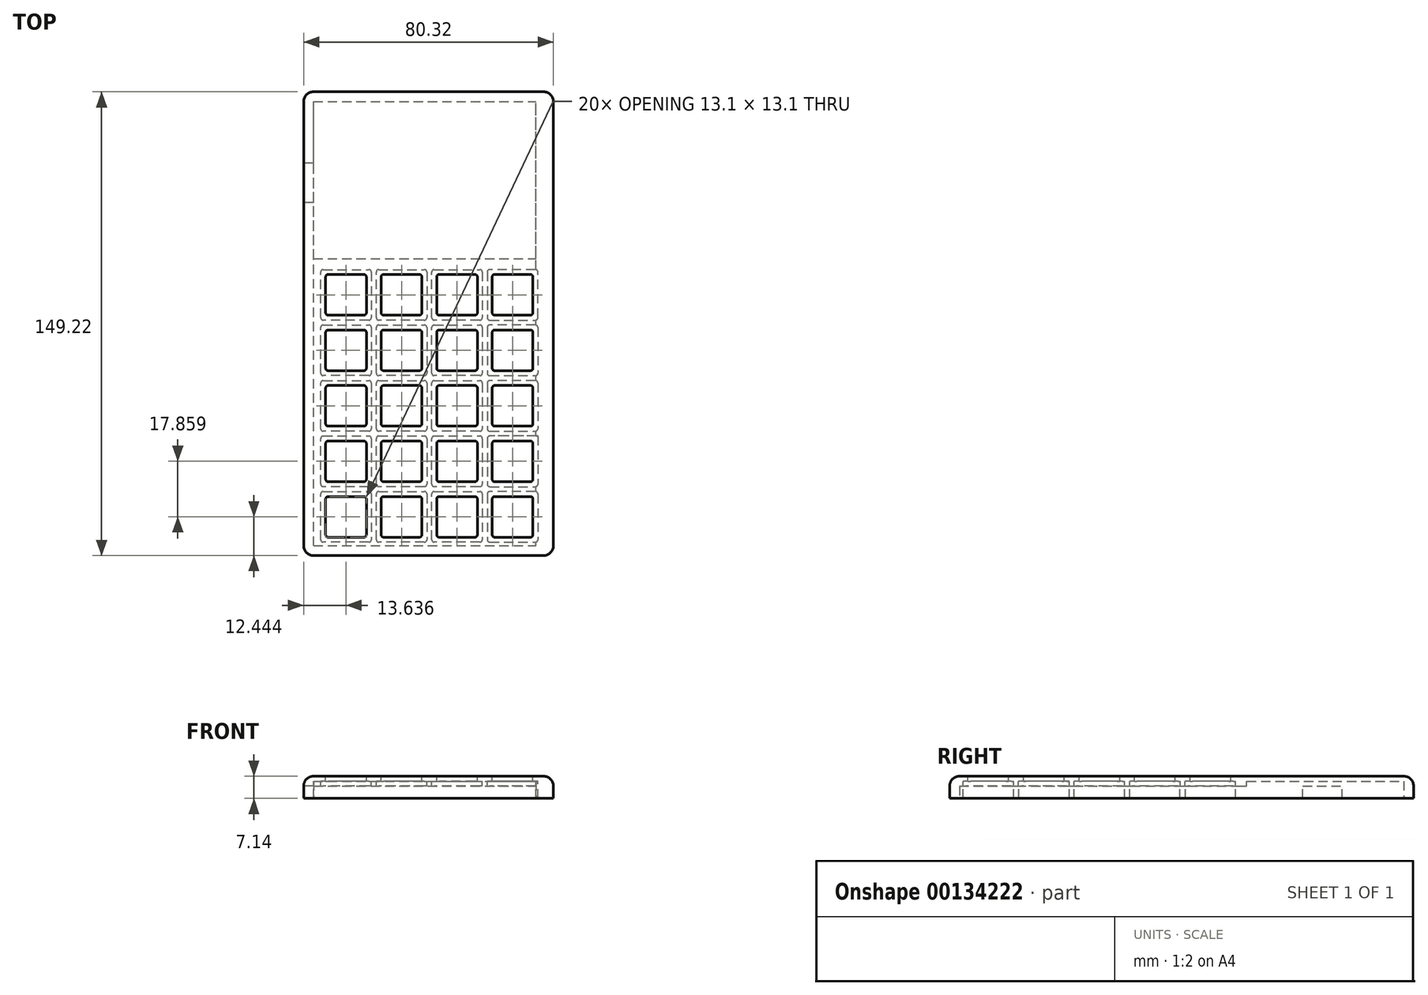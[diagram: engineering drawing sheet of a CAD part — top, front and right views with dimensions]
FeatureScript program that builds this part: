
annotation { "Feature Type Name" : "Feature", "Feature Type Description" : "" }
export const myFeature = defineFeature(function(context is Context, id is Id, definition is map)
    precondition{}
    {
        {
            var Q0;
            Q0=qCreatedBy(makeId("Top.planeOp"),FACE);
            var sketch = newSketch(context, id + "F0", { "sketchPlane" : qUnion([Q0])});
            skLineSegment(sketch, "E0.bottom", {"start": v(40.16, 74.61) * mm, "end": v(-40.16, 74.61) * mm});
            skLineSegment(sketch, "E0.top", {"start": v(40.16, -74.61) * mm, "end": v(-40.16, -74.61) * mm});
            skLineSegment(sketch, "E0.left", {"start": v(40.16, 74.61) * mm, "end": v(40.16, -74.61) * mm});
            skLineSegment(sketch, "E0.right", {"start": v(-40.16, 74.61) * mm, "end": v(-40.16, -74.61) * mm});
            skPoint(sketch, "E0.middle", {"position": v(0, 0) * mm});
            skSolve(sketch);
        }
        {
            var Q0;
            Q0 = qSketchRegion(id + "F0", true);
            extrude(context, id + "F1", {"entities" : qUnion([Q0]), "depth" : 7.14 * mm});
        }
        {
            var Q0;
            Q0=makeQuery(id+"F1.opExtrude","CAP_EDGE",EDGE,{"disambiguationData":[OSD([sQuery(id+"F0.wireOp",EDGE,"E0.right")])],"isStart":false});
            var Q1;
            Q1=makeQuery(id+"F1.opExtrude","CAP_EDGE",EDGE,{"disambiguationData":[OSD([sQuery(id+"F0.wireOp",EDGE,"E0.bottom")])],"isStart":false});
            var Q2;
            Q2=makeQuery(id+"F1.opExtrude","CAP_EDGE",EDGE,{"disambiguationData":[OSD([sQuery(id+"F0.wireOp",EDGE,"E0.left")])],"isStart":false});
            var Q3;
            Q3=makeQuery(id+"F1.opExtrude","CAP_EDGE",EDGE,{"disambiguationData":[OSD([sQuery(id+"F0.wireOp",EDGE,"E0.top")])],"isStart":false});
            fillet(context, id + "F2", {"entities" : qUnion([Q0, Q1, Q2, Q3]), "radius" : 3.17 * mm, "tangentPropagation" : true, "allowEdgeOverflow" : false});
        }
        {
            var Q0;
            Q0=makeQuery(id+"F1.opExtrude","SWEPT_EDGE",EDGE,{"disambiguationData":[OSD([sQuery(id+"F0.wireOp",EDGE,"E0.bottom"),sQuery(id+"F0.wireOp",EDGE,"E0.left")])]});
            var Q1;
            Q1=makeQuery(id+"F1.opExtrude","SWEPT_EDGE",EDGE,{"disambiguationData":[OSD([sQuery(id+"F0.wireOp",EDGE,"E0.top"),sQuery(id+"F0.wireOp",EDGE,"E0.left")])]});
            var Q2;
            Q2=makeQuery(id+"F1.opExtrude","SWEPT_EDGE",EDGE,{"disambiguationData":[OSD([sQuery(id+"F0.wireOp",EDGE,"E0.top"),sQuery(id+"F0.wireOp",EDGE,"E0.right")])]});
            var Q3;
            Q3=makeQuery(id+"F1.opExtrude","SWEPT_EDGE",EDGE,{"disambiguationData":[OSD([sQuery(id+"F0.wireOp",EDGE,"E0.bottom"),sQuery(id+"F0.wireOp",EDGE,"E0.right")])]});
            fillet(context, id + "F3", {"entities" : qUnion([Q0, Q1, Q2, Q3]), "radius" : 3.17 * mm, "tangentPropagation" : true, "allowEdgeOverflow" : false});
        }
        {
            var Q0;
            Q0=makeQuery(id+"F1.opExtrude","CAP_FACE",FACE,{"disambiguationData":[OSD([sQuery(id+"F0.wireOp",EDGE,"E0.bottom"),sQuery(id+"F0.wireOp",EDGE,"E0.top"),sQuery(id+"F0.wireOp",EDGE,"E0.left"),sQuery(id+"F0.wireOp",EDGE,"E0.right")])],"isStart":true});
            var sketch = newSketch(context, id + "F4", { "sketchPlane" : qUnion([Q0])});
            skLineSegment(sketch, "E1.0.0", {"start": v(40.16, -71.44) * mm, "end": v(40.16, 71.44) * mm});
            skArc(sketch, "E1.0.1", {"start": v(40.16, 71.44) * mm, "mid": v(39.23, 73.68) * mm, "end": v(36.99, 74.61) * mm});
            skLineSegment(sketch, "E1.0.2", {"start": v(36.99, 74.61) * mm, "end": v(-36.99, 74.61) * mm});
            skArc(sketch, "E1.0.3", {"start": v(-36.99, 74.61) * mm, "mid": v(-39.23, 73.68) * mm, "end": v(-40.16, 71.44) * mm});
            skLineSegment(sketch, "E1.0.4", {"start": v(-40.16, 71.44) * mm, "end": v(-40.16, -71.44) * mm});
            skArc(sketch, "E1.0.5", {"start": v(-40.16, -71.44) * mm, "mid": v(-39.23, -73.68) * mm, "end": v(-36.99, -74.61) * mm});
            skLineSegment(sketch, "E1.0.6", {"start": v(-36.99, -74.61) * mm, "end": v(36.99, -74.61) * mm});
            skArc(sketch, "E1.0.7", {"start": v(36.99, -74.61) * mm, "mid": v(39.23, -73.68) * mm, "end": v(40.16, -71.44) * mm});
            skLineSegment(sketch, "E2.bottom", {"start": v(-36.99, 71.44) * mm, "end": v(34.6, 71.44) * mm});
            skLineSegment(sketch, "E2.top", {"start": v(-36.99, -71.44) * mm, "end": v(34.6, -71.44) * mm});
            skLineSegment(sketch, "E2.left", {"start": v(-36.99, 71.44) * mm, "end": v(-36.99, -71.44) * mm});
            skLineSegment(sketch, "E2.right", {"start": v(34.6, 71.44) * mm, "end": v(34.6, -71.44) * mm});
            skSolve(sketch);
        }
        {
            var Q0;
            Q0=makeQuery(id+"F4.imprint","IMPRINT",FACE,{"disambiguationData":[TD([[makeQuery(id+"F4.imprint","IMPRINT",EDGE,{"derivedFrom":sQuery(id+"F4.wireOp",EDGE,"E2.bottom")}),-1.0]])]});
            extrude(context, id + "F5", {"entities" : qUnion([Q0]), "operationType" : NewBodyOperationType.REMOVE, "oppositeDirection" : true, "depth" : 5.56 * mm});
        }
        {
            var Q0;
            Q0=makeQuery(id+"F1.opExtrude","CAP_FACE",FACE,{"disambiguationData":[OSD([sQuery(id+"F0.wireOp",EDGE,"E0.bottom"),sQuery(id+"F0.wireOp",EDGE,"E0.top"),sQuery(id+"F0.wireOp",EDGE,"E0.left"),sQuery(id+"F0.wireOp",EDGE,"E0.right")])],"isStart":false});
            var sketch = newSketch(context, id + "F6", { "sketchPlane" : qUnion([Q0])});
            skLineSegment(sketch, "E3.0.0", {"start": v(-36.99, -71.44) * mm, "end": v(-36.99, -71.44) * mm});
            skLineSegment(sketch, "E3.0.1", {"start": v(-36.99, -71.44) * mm, "end": v(36.99, -71.44) * mm});
            skLineSegment(sketch, "E3.0.2", {"start": v(36.99, -71.44) * mm, "end": v(36.99, -71.44) * mm});
            skLineSegment(sketch, "E3.0.3", {"start": v(36.99, -71.44) * mm, "end": v(36.99, 71.44) * mm});
            skArc(sketch, "E3.0.4", {"start": v(35.08, 71.44) * mm, "mid": v(36.04, 71.7) * mm, "end": v(36.99, 71.44) * mm});
            skLineSegment(sketch, "E3.0.5", {"start": v(35.08, 71.44) * mm, "end": v(-35.08, 71.44) * mm});
            skArc(sketch, "E3.0.6", {"start": v(-36.99, 71.44) * mm, "mid": v(-36.04, 71.7) * mm, "end": v(-35.08, 71.44) * mm});
            skLineSegment(sketch, "E3.0.7", {"start": v(-36.99, 71.44) * mm, "end": v(-36.99, -71.44) * mm});
            skLineSegment(sketch, "E4.0.0", {"start": v(40.16, -71.44) * mm, "end": v(40.16, 71.44) * mm});
            skLineSegment(sketch, "E4.0.1", {"start": v(40.16, 71.44) * mm, "end": v(36.99, 71.44) * mm});
            skLineSegment(sketch, "E4.0.3", {"start": v(36.99, -71.44) * mm, "end": v(40.16, -71.44) * mm});
            skLineSegment(sketch, "E5.0.2", {"start": v(36.99, -71.44) * mm, "end": v(36.99, -74.61) * mm});
            skArc(sketch, "E5.0.3", {"start": v(36.99, -74.61) * mm, "mid": v(39.23, -73.68) * mm, "end": v(40.16, -71.44) * mm});
            skLineSegment(sketch, "E6.0.0", {"start": v(-36.99, -74.61) * mm, "end": v(36.99, -74.61) * mm});
            skLineSegment(sketch, "E6.0.1", {"start": v(36.99, -74.61) * mm, "end": v(36.99, -71.44) * mm});
            skLineSegment(sketch, "E6.0.3", {"start": v(-36.99, -71.44) * mm, "end": v(-36.99, -74.61) * mm});
            skLineSegment(sketch, "E7.0.2", {"start": v(-36.99, -71.44) * mm, "end": v(-40.16, -71.44) * mm});
            skArc(sketch, "E7.0.3", {"start": v(-40.16, -71.44) * mm, "mid": v(-39.23, -73.68) * mm, "end": v(-36.99, -74.61) * mm});
            skLineSegment(sketch, "E8.0.0", {"start": v(-40.16, -71.44) * mm, "end": v(-40.16, 71.44) * mm});
            skLineSegment(sketch, "E8.0.1", {"start": v(-40.16, -71.44) * mm, "end": v(-36.99, -71.44) * mm});
            skLineSegment(sketch, "E8.0.2", {"start": v(-36.99, -71.44) * mm, "end": v(-36.99, 71.44) * mm});
            skLineSegment(sketch, "E8.0.3", {"start": v(-36.99, 71.44) * mm, "end": v(-40.16, 71.44) * mm});
            skLineSegment(sketch, "E9.bottom", {"start": v(27.04, -74.61) * mm, "end": v(40.16, -74.61) * mm});
            skLineSegment(sketch, "E9.top", {"start": v(27.04, -62.17) * mm, "end": v(40.16, -62.17) * mm});
            skLineSegment(sketch, "E9.left", {"start": v(27.04, -74.61) * mm, "end": v(27.04, -62.17) * mm});
            skLineSegment(sketch, "E9.right", {"start": v(40.16, -74.61) * mm, "end": v(40.16, -62.17) * mm});
            skLineSegment(sketch, "E10.bottom", {"start": v(21.29, -68.71) * mm, "end": v(32.8, -68.71) * mm});
            skLineSegment(sketch, "E10.top", {"start": v(21.29, -55.62) * mm, "end": v(32.8, -55.62) * mm});
            skLineSegment(sketch, "E10.left", {"start": v(20.5, -67.92) * mm, "end": v(20.5, -56.41) * mm});
            skLineSegment(sketch, "E10.right", {"start": v(33.6, -67.92) * mm, "end": v(33.6, -56.41) * mm});
            skPoint(sketch, "E10.middle", {"position": v(27.04, -62.17) * mm});
            skPoint(sketch, "E11.visualSharp", {"position": v(20.5, -55.62) * mm});
            skArc(sketch, "E11.filletArc", {"start": v(21.29, -55.62) * mm, "mid": v(20.73, -55.85) * mm, "end": v(20.5, -56.41) * mm});
            skPoint(sketch, "E12.visualSharp", {"position": v(33.6, -55.62) * mm});
            skArc(sketch, "E12.filletArc", {"start": v(33.6, -56.41) * mm, "mid": v(33.36, -55.85) * mm, "end": v(32.8, -55.62) * mm});
            skPoint(sketch, "E13.visualSharp", {"position": v(33.6, -68.71) * mm});
            skArc(sketch, "E13.filletArc", {"start": v(32.8, -68.71) * mm, "mid": v(33.36, -68.48) * mm, "end": v(33.6, -67.92) * mm});
            skPoint(sketch, "E14.visualSharp", {"position": v(20.5, -68.71) * mm});
            skArc(sketch, "E14.filletArc", {"start": v(20.5, -67.92) * mm, "mid": v(20.73, -68.48) * mm, "end": v(21.29, -68.71) * mm});
            skLineSegment(sketch, "E15", {"start": v(27.04, -62.17) * mm, "end": v(18.31, -62.17) * mm});
            skLineSegment(sketch, "E16", {"start": v(18.31, -55.46) * mm, "end": v(18.31, -68.4) * mm, "construction": true});
            skLineSegment(sketch, "E17.1.0.0", {"start": v(2.64, -67.92) * mm, "end": v(2.64, -56.41) * mm});
            skArc(sketch, "E17.1.0.1", {"start": v(3.43, -55.62) * mm, "mid": v(2.87, -55.85) * mm, "end": v(2.64, -56.41) * mm});
            skLineSegment(sketch, "E17.1.0.2", {"start": v(3.43, -55.62) * mm, "end": v(14.94, -55.62) * mm});
            skArc(sketch, "E17.1.0.3", {"start": v(15.74, -56.41) * mm, "mid": v(15.5, -55.85) * mm, "end": v(14.94, -55.62) * mm});
            skLineSegment(sketch, "E17.1.0.4", {"start": v(15.74, -67.92) * mm, "end": v(15.74, -56.41) * mm});
            skArc(sketch, "E17.1.0.5", {"start": v(14.94, -68.71) * mm, "mid": v(15.5, -68.48) * mm, "end": v(15.74, -67.92) * mm});
            skLineSegment(sketch, "E17.1.0.6", {"start": v(3.43, -68.71) * mm, "end": v(14.94, -68.71) * mm});
            skArc(sketch, "E17.1.0.7", {"start": v(2.64, -67.92) * mm, "mid": v(2.87, -68.48) * mm, "end": v(3.43, -68.71) * mm});
            skLineSegment(sketch, "E17.2.0.0", {"start": v(-15.22, -67.92) * mm, "end": v(-15.22, -56.41) * mm});
            skArc(sketch, "E17.2.0.1", {"start": v(-14.42, -55.62) * mm, "mid": v(-14.98, -55.85) * mm, "end": v(-15.22, -56.41) * mm});
            skLineSegment(sketch, "E17.2.0.2", {"start": v(-14.42, -55.62) * mm, "end": v(-2.91, -55.62) * mm});
            skArc(sketch, "E17.2.0.3", {"start": v(-2.12, -56.41) * mm, "mid": v(-2.35, -55.85) * mm, "end": v(-2.91, -55.62) * mm});
            skLineSegment(sketch, "E17.2.0.4", {"start": v(-2.12, -67.92) * mm, "end": v(-2.12, -56.41) * mm});
            skArc(sketch, "E17.2.0.5", {"start": v(-2.91, -68.71) * mm, "mid": v(-2.35, -68.48) * mm, "end": v(-2.12, -67.92) * mm});
            skLineSegment(sketch, "E17.2.0.6", {"start": v(-14.42, -68.71) * mm, "end": v(-2.91, -68.71) * mm});
            skArc(sketch, "E17.2.0.7", {"start": v(-15.22, -67.92) * mm, "mid": v(-14.98, -68.48) * mm, "end": v(-14.42, -68.71) * mm});
            skLineSegment(sketch, "E17.3.0.0", {"start": v(-33.07, -67.92) * mm, "end": v(-33.07, -56.41) * mm});
            skArc(sketch, "E17.3.0.1", {"start": v(-32.28, -55.62) * mm, "mid": v(-32.84, -55.85) * mm, "end": v(-33.07, -56.41) * mm});
            skLineSegment(sketch, "E17.3.0.2", {"start": v(-32.28, -55.62) * mm, "end": v(-20.77, -55.62) * mm});
            skArc(sketch, "E17.3.0.3", {"start": v(-19.98, -56.41) * mm, "mid": v(-20.2, -55.85) * mm, "end": v(-20.77, -55.62) * mm});
            skLineSegment(sketch, "E17.3.0.4", {"start": v(-19.98, -67.92) * mm, "end": v(-19.98, -56.41) * mm});
            skArc(sketch, "E17.3.0.5", {"start": v(-20.77, -68.71) * mm, "mid": v(-20.2, -68.48) * mm, "end": v(-19.98, -67.92) * mm});
            skLineSegment(sketch, "E17.3.0.6", {"start": v(-32.28, -68.71) * mm, "end": v(-20.77, -68.71) * mm});
            skArc(sketch, "E17.3.0.7", {"start": v(-33.07, -67.92) * mm, "mid": v(-32.84, -68.48) * mm, "end": v(-32.28, -68.71) * mm});
            skLineSegment(sketch, "E17.direction1", {"start": v(20.5, -67.92) * mm, "end": v(2.64, -67.92) * mm, "construction": true});
            skLineSegment(sketch, "E18", {"start": v(-26.52, -55.62) * mm, "end": v(-26.52, -68.71) * mm});
            skLineSegment(sketch, "E19.0.1.0", {"start": v(-33.07, -50.06) * mm, "end": v(-33.07, -38.55) * mm});
            skArc(sketch, "E19.0.1.1", {"start": v(-32.28, -37.76) * mm, "mid": v(-32.84, -38) * mm, "end": v(-33.07, -38.55) * mm});
            skLineSegment(sketch, "E19.0.1.2", {"start": v(-32.28, -37.76) * mm, "end": v(-20.77, -37.76) * mm});
            skArc(sketch, "E19.0.1.3", {"start": v(-33.07, -50.06) * mm, "mid": v(-32.84, -50.62) * mm, "end": v(-32.28, -50.86) * mm});
            skLineSegment(sketch, "E19.0.1.4", {"start": v(-32.28, -50.86) * mm, "end": v(-20.77, -50.86) * mm});
            skArc(sketch, "E19.0.1.5", {"start": v(-20.77, -50.86) * mm, "mid": v(-20.2, -50.62) * mm, "end": v(-19.98, -50.06) * mm});
            skLineSegment(sketch, "E19.0.1.6", {"start": v(-19.98, -50.06) * mm, "end": v(-19.98, -38.55) * mm});
            skArc(sketch, "E19.0.1.7", {"start": v(-19.98, -38.55) * mm, "mid": v(-20.2, -38) * mm, "end": v(-20.77, -37.76) * mm});
            skArc(sketch, "E19.0.1.8", {"start": v(-14.42, -37.76) * mm, "mid": v(-14.98, -38) * mm, "end": v(-15.22, -38.55) * mm});
            skLineSegment(sketch, "E19.0.1.9", {"start": v(-15.22, -50.06) * mm, "end": v(-15.22, -38.55) * mm});
            skArc(sketch, "E19.0.1.10", {"start": v(-15.22, -50.06) * mm, "mid": v(-14.98, -50.62) * mm, "end": v(-14.42, -50.86) * mm});
            skLineSegment(sketch, "E19.0.1.11", {"start": v(-14.42, -50.86) * mm, "end": v(-2.91, -50.86) * mm});
            skArc(sketch, "E19.0.1.12", {"start": v(-2.91, -50.86) * mm, "mid": v(-2.35, -50.62) * mm, "end": v(-2.12, -50.06) * mm});
            skLineSegment(sketch, "E19.0.1.13", {"start": v(-2.12, -50.06) * mm, "end": v(-2.12, -38.55) * mm});
            skArc(sketch, "E19.0.1.14", {"start": v(-2.12, -38.55) * mm, "mid": v(-2.35, -38) * mm, "end": v(-2.91, -37.76) * mm});
            skLineSegment(sketch, "E19.0.1.15", {"start": v(-14.42, -37.76) * mm, "end": v(-2.91, -37.76) * mm});
            skLineSegment(sketch, "E19.0.1.16", {"start": v(2.64, -50.06) * mm, "end": v(2.64, -38.55) * mm});
            skArc(sketch, "E19.0.1.17", {"start": v(3.43, -37.76) * mm, "mid": v(2.87, -38) * mm, "end": v(2.64, -38.55) * mm});
            skLineSegment(sketch, "E19.0.1.18", {"start": v(3.43, -37.76) * mm, "end": v(14.94, -37.76) * mm});
            skArc(sketch, "E19.0.1.19", {"start": v(15.74, -38.55) * mm, "mid": v(15.5, -38) * mm, "end": v(14.94, -37.76) * mm});
            skLineSegment(sketch, "E19.0.1.20", {"start": v(15.74, -50.06) * mm, "end": v(15.74, -38.55) * mm});
            skArc(sketch, "E19.0.1.21", {"start": v(14.94, -50.86) * mm, "mid": v(15.5, -50.62) * mm, "end": v(15.74, -50.06) * mm});
            skLineSegment(sketch, "E19.0.1.22", {"start": v(3.43, -50.86) * mm, "end": v(14.94, -50.86) * mm});
            skArc(sketch, "E19.0.1.23", {"start": v(2.64, -50.06) * mm, "mid": v(2.87, -50.62) * mm, "end": v(3.43, -50.86) * mm});
            skArc(sketch, "E19.0.1.24", {"start": v(20.5, -50.06) * mm, "mid": v(20.73, -50.62) * mm, "end": v(21.29, -50.86) * mm});
            skLineSegment(sketch, "E19.0.1.25", {"start": v(20.5, -50.06) * mm, "end": v(20.5, -38.55) * mm});
            skArc(sketch, "E19.0.1.26", {"start": v(21.29, -37.76) * mm, "mid": v(20.73, -38) * mm, "end": v(20.5, -38.55) * mm});
            skLineSegment(sketch, "E19.0.1.27", {"start": v(21.29, -37.76) * mm, "end": v(32.8, -37.76) * mm});
            skArc(sketch, "E19.0.1.28", {"start": v(33.6, -38.55) * mm, "mid": v(33.36, -38) * mm, "end": v(32.8, -37.76) * mm});
            skLineSegment(sketch, "E19.0.1.29", {"start": v(33.6, -50.06) * mm, "end": v(33.6, -38.55) * mm});
            skArc(sketch, "E19.0.1.30", {"start": v(32.8, -50.86) * mm, "mid": v(33.36, -50.62) * mm, "end": v(33.6, -50.06) * mm});
            skLineSegment(sketch, "E19.0.1.31", {"start": v(21.29, -50.86) * mm, "end": v(32.8, -50.86) * mm});
            skLineSegment(sketch, "E19.0.2.0", {"start": v(-33.07, -32.2) * mm, "end": v(-33.07, -20.7) * mm});
            skArc(sketch, "E19.0.2.1", {"start": v(-32.28, -19.9) * mm, "mid": v(-32.84, -20.13) * mm, "end": v(-33.07, -20.7) * mm});
            skLineSegment(sketch, "E19.0.2.2", {"start": v(-32.28, -19.9) * mm, "end": v(-20.77, -19.9) * mm});
            skArc(sketch, "E19.0.2.3", {"start": v(-33.07, -32.2) * mm, "mid": v(-32.84, -32.76) * mm, "end": v(-32.28, -33) * mm});
            skLineSegment(sketch, "E19.0.2.4", {"start": v(-32.28, -33) * mm, "end": v(-20.77, -33) * mm});
            skArc(sketch, "E19.0.2.5", {"start": v(-20.77, -33) * mm, "mid": v(-20.2, -32.76) * mm, "end": v(-19.98, -32.2) * mm});
            skLineSegment(sketch, "E19.0.2.6", {"start": v(-19.98, -32.2) * mm, "end": v(-19.98, -20.7) * mm});
            skArc(sketch, "E19.0.2.7", {"start": v(-19.98, -20.7) * mm, "mid": v(-20.2, -20.13) * mm, "end": v(-20.77, -19.9) * mm});
            skArc(sketch, "E19.0.2.8", {"start": v(-14.42, -19.9) * mm, "mid": v(-14.98, -20.13) * mm, "end": v(-15.22, -20.7) * mm});
            skLineSegment(sketch, "E19.0.2.9", {"start": v(-15.22, -32.2) * mm, "end": v(-15.22, -20.7) * mm});
            skArc(sketch, "E19.0.2.10", {"start": v(-15.22, -32.2) * mm, "mid": v(-14.98, -32.76) * mm, "end": v(-14.42, -33) * mm});
            skLineSegment(sketch, "E19.0.2.11", {"start": v(-14.42, -33) * mm, "end": v(-2.91, -33) * mm});
            skArc(sketch, "E19.0.2.12", {"start": v(-2.91, -33) * mm, "mid": v(-2.35, -32.76) * mm, "end": v(-2.12, -32.2) * mm});
            skLineSegment(sketch, "E19.0.2.13", {"start": v(-2.12, -32.2) * mm, "end": v(-2.12, -20.7) * mm});
            skArc(sketch, "E19.0.2.14", {"start": v(-2.12, -20.7) * mm, "mid": v(-2.35, -20.13) * mm, "end": v(-2.91, -19.9) * mm});
            skLineSegment(sketch, "E19.0.2.15", {"start": v(-14.42, -19.9) * mm, "end": v(-2.91, -19.9) * mm});
            skLineSegment(sketch, "E19.0.2.16", {"start": v(2.64, -32.2) * mm, "end": v(2.64, -20.7) * mm});
            skArc(sketch, "E19.0.2.17", {"start": v(3.43, -19.9) * mm, "mid": v(2.87, -20.13) * mm, "end": v(2.64, -20.7) * mm});
            skLineSegment(sketch, "E19.0.2.18", {"start": v(3.43, -19.9) * mm, "end": v(14.94, -19.9) * mm});
            skArc(sketch, "E19.0.2.19", {"start": v(15.74, -20.7) * mm, "mid": v(15.5, -20.13) * mm, "end": v(14.94, -19.9) * mm});
            skLineSegment(sketch, "E19.0.2.20", {"start": v(15.74, -32.2) * mm, "end": v(15.74, -20.7) * mm});
            skArc(sketch, "E19.0.2.21", {"start": v(14.94, -33) * mm, "mid": v(15.5, -32.76) * mm, "end": v(15.74, -32.2) * mm});
            skLineSegment(sketch, "E19.0.2.22", {"start": v(3.43, -33) * mm, "end": v(14.94, -33) * mm});
            skArc(sketch, "E19.0.2.23", {"start": v(2.64, -32.2) * mm, "mid": v(2.87, -32.76) * mm, "end": v(3.43, -33) * mm});
            skArc(sketch, "E19.0.2.24", {"start": v(20.5, -32.2) * mm, "mid": v(20.73, -32.76) * mm, "end": v(21.29, -33) * mm});
            skLineSegment(sketch, "E19.0.2.25", {"start": v(20.5, -32.2) * mm, "end": v(20.5, -20.7) * mm});
            skArc(sketch, "E19.0.2.26", {"start": v(21.29, -19.9) * mm, "mid": v(20.73, -20.13) * mm, "end": v(20.5, -20.7) * mm});
            skLineSegment(sketch, "E19.0.2.27", {"start": v(21.29, -19.9) * mm, "end": v(32.8, -19.9) * mm});
            skArc(sketch, "E19.0.2.28", {"start": v(33.6, -20.7) * mm, "mid": v(33.36, -20.13) * mm, "end": v(32.8, -19.9) * mm});
            skLineSegment(sketch, "E19.0.2.29", {"start": v(33.6, -32.2) * mm, "end": v(33.6, -20.7) * mm});
            skArc(sketch, "E19.0.2.30", {"start": v(32.8, -33) * mm, "mid": v(33.36, -32.76) * mm, "end": v(33.6, -32.2) * mm});
            skLineSegment(sketch, "E19.0.2.31", {"start": v(21.29, -33) * mm, "end": v(32.8, -33) * mm});
            skLineSegment(sketch, "E19.0.3.0", {"start": v(-33.07, -14.34) * mm, "end": v(-33.07, -2.83) * mm});
            skArc(sketch, "E19.0.3.1", {"start": v(-32.28, -2.04) * mm, "mid": v(-32.84, -2.27) * mm, "end": v(-33.07, -2.83) * mm});
            skLineSegment(sketch, "E19.0.3.2", {"start": v(-32.28, -2.04) * mm, "end": v(-20.77, -2.04) * mm});
            skArc(sketch, "E19.0.3.3", {"start": v(-33.07, -14.34) * mm, "mid": v(-32.84, -14.9) * mm, "end": v(-32.28, -15.14) * mm});
            skLineSegment(sketch, "E19.0.3.4", {"start": v(-32.28, -15.14) * mm, "end": v(-20.77, -15.14) * mm});
            skArc(sketch, "E19.0.3.5", {"start": v(-20.77, -15.14) * mm, "mid": v(-20.2, -14.9) * mm, "end": v(-19.98, -14.34) * mm});
            skLineSegment(sketch, "E19.0.3.6", {"start": v(-19.98, -14.34) * mm, "end": v(-19.98, -2.83) * mm});
            skArc(sketch, "E19.0.3.7", {"start": v(-19.98, -2.83) * mm, "mid": v(-20.2, -2.27) * mm, "end": v(-20.77, -2.04) * mm});
            skArc(sketch, "E19.0.3.8", {"start": v(-14.42, -2.04) * mm, "mid": v(-14.98, -2.27) * mm, "end": v(-15.22, -2.83) * mm});
            skLineSegment(sketch, "E19.0.3.9", {"start": v(-15.22, -14.34) * mm, "end": v(-15.22, -2.83) * mm});
            skArc(sketch, "E19.0.3.10", {"start": v(-15.22, -14.34) * mm, "mid": v(-14.98, -14.9) * mm, "end": v(-14.42, -15.14) * mm});
            skLineSegment(sketch, "E19.0.3.11", {"start": v(-14.42, -15.14) * mm, "end": v(-2.91, -15.14) * mm});
            skArc(sketch, "E19.0.3.12", {"start": v(-2.91, -15.14) * mm, "mid": v(-2.35, -14.9) * mm, "end": v(-2.12, -14.34) * mm});
            skLineSegment(sketch, "E19.0.3.13", {"start": v(-2.12, -14.34) * mm, "end": v(-2.12, -2.83) * mm});
            skArc(sketch, "E19.0.3.14", {"start": v(-2.12, -2.83) * mm, "mid": v(-2.35, -2.27) * mm, "end": v(-2.91, -2.04) * mm});
            skLineSegment(sketch, "E19.0.3.15", {"start": v(-14.42, -2.04) * mm, "end": v(-2.91, -2.04) * mm});
            skLineSegment(sketch, "E19.0.3.16", {"start": v(2.64, -14.34) * mm, "end": v(2.64, -2.83) * mm});
            skArc(sketch, "E19.0.3.17", {"start": v(3.43, -2.04) * mm, "mid": v(2.87, -2.27) * mm, "end": v(2.64, -2.83) * mm});
            skLineSegment(sketch, "E19.0.3.18", {"start": v(3.43, -2.04) * mm, "end": v(14.94, -2.04) * mm});
            skArc(sketch, "E19.0.3.19", {"start": v(15.74, -2.83) * mm, "mid": v(15.5, -2.27) * mm, "end": v(14.94, -2.04) * mm});
            skLineSegment(sketch, "E19.0.3.20", {"start": v(15.74, -14.34) * mm, "end": v(15.74, -2.83) * mm});
            skArc(sketch, "E19.0.3.21", {"start": v(14.94, -15.14) * mm, "mid": v(15.5, -14.9) * mm, "end": v(15.74, -14.34) * mm});
            skLineSegment(sketch, "E19.0.3.22", {"start": v(3.43, -15.14) * mm, "end": v(14.94, -15.14) * mm});
            skArc(sketch, "E19.0.3.23", {"start": v(2.64, -14.34) * mm, "mid": v(2.87, -14.9) * mm, "end": v(3.43, -15.14) * mm});
            skArc(sketch, "E19.0.3.24", {"start": v(20.5, -14.34) * mm, "mid": v(20.73, -14.9) * mm, "end": v(21.29, -15.14) * mm});
            skLineSegment(sketch, "E19.0.3.25", {"start": v(20.5, -14.34) * mm, "end": v(20.5, -2.83) * mm});
            skArc(sketch, "E19.0.3.26", {"start": v(21.29, -2.04) * mm, "mid": v(20.73, -2.27) * mm, "end": v(20.5, -2.83) * mm});
            skLineSegment(sketch, "E19.0.3.27", {"start": v(21.29, -2.04) * mm, "end": v(32.8, -2.04) * mm});
            skArc(sketch, "E19.0.3.28", {"start": v(33.6, -2.83) * mm, "mid": v(33.36, -2.27) * mm, "end": v(32.8, -2.04) * mm});
            skLineSegment(sketch, "E19.0.3.29", {"start": v(33.6, -14.34) * mm, "end": v(33.6, -2.83) * mm});
            skArc(sketch, "E19.0.3.30", {"start": v(32.8, -15.14) * mm, "mid": v(33.36, -14.9) * mm, "end": v(33.6, -14.34) * mm});
            skLineSegment(sketch, "E19.0.3.31", {"start": v(21.29, -15.14) * mm, "end": v(32.8, -15.14) * mm});
            skLineSegment(sketch, "E19.0.4.0", {"start": v(-33.07, 3.52) * mm, "end": v(-33.07, 15.03) * mm});
            skArc(sketch, "E19.0.4.1", {"start": v(-32.28, 15.82) * mm, "mid": v(-32.84, 15.59) * mm, "end": v(-33.07, 15.03) * mm});
            skLineSegment(sketch, "E19.0.4.2", {"start": v(-32.28, 15.82) * mm, "end": v(-20.77, 15.82) * mm});
            skArc(sketch, "E19.0.4.3", {"start": v(-33.07, 3.52) * mm, "mid": v(-32.84, 2.96) * mm, "end": v(-32.28, 2.72) * mm});
            skLineSegment(sketch, "E19.0.4.4", {"start": v(-32.28, 2.72) * mm, "end": v(-20.77, 2.72) * mm});
            skArc(sketch, "E19.0.4.5", {"start": v(-20.77, 2.72) * mm, "mid": v(-20.2, 2.96) * mm, "end": v(-19.98, 3.52) * mm});
            skLineSegment(sketch, "E19.0.4.6", {"start": v(-19.98, 3.52) * mm, "end": v(-19.98, 15.03) * mm});
            skArc(sketch, "E19.0.4.7", {"start": v(-19.98, 15.03) * mm, "mid": v(-20.2, 15.59) * mm, "end": v(-20.77, 15.82) * mm});
            skArc(sketch, "E19.0.4.8", {"start": v(-14.42, 15.82) * mm, "mid": v(-14.98, 15.59) * mm, "end": v(-15.22, 15.03) * mm});
            skLineSegment(sketch, "E19.0.4.9", {"start": v(-15.22, 3.52) * mm, "end": v(-15.22, 15.03) * mm});
            skArc(sketch, "E19.0.4.10", {"start": v(-15.22, 3.52) * mm, "mid": v(-14.98, 2.96) * mm, "end": v(-14.42, 2.72) * mm});
            skLineSegment(sketch, "E19.0.4.11", {"start": v(-14.42, 2.72) * mm, "end": v(-2.91, 2.72) * mm});
            skArc(sketch, "E19.0.4.12", {"start": v(-2.91, 2.72) * mm, "mid": v(-2.35, 2.96) * mm, "end": v(-2.12, 3.52) * mm});
            skLineSegment(sketch, "E19.0.4.13", {"start": v(-2.12, 3.52) * mm, "end": v(-2.12, 15.03) * mm});
            skArc(sketch, "E19.0.4.14", {"start": v(-2.12, 15.03) * mm, "mid": v(-2.35, 15.59) * mm, "end": v(-2.91, 15.82) * mm});
            skLineSegment(sketch, "E19.0.4.15", {"start": v(-14.42, 15.82) * mm, "end": v(-2.91, 15.82) * mm});
            skLineSegment(sketch, "E19.0.4.16", {"start": v(2.64, 3.52) * mm, "end": v(2.64, 15.03) * mm});
            skArc(sketch, "E19.0.4.17", {"start": v(3.43, 15.82) * mm, "mid": v(2.87, 15.59) * mm, "end": v(2.64, 15.03) * mm});
            skLineSegment(sketch, "E19.0.4.18", {"start": v(3.43, 15.82) * mm, "end": v(14.94, 15.82) * mm});
            skArc(sketch, "E19.0.4.19", {"start": v(15.74, 15.03) * mm, "mid": v(15.5, 15.59) * mm, "end": v(14.94, 15.82) * mm});
            skLineSegment(sketch, "E19.0.4.20", {"start": v(15.74, 3.52) * mm, "end": v(15.74, 15.03) * mm});
            skArc(sketch, "E19.0.4.21", {"start": v(14.94, 2.72) * mm, "mid": v(15.5, 2.96) * mm, "end": v(15.74, 3.52) * mm});
            skLineSegment(sketch, "E19.0.4.22", {"start": v(3.43, 2.72) * mm, "end": v(14.94, 2.72) * mm});
            skArc(sketch, "E19.0.4.23", {"start": v(2.64, 3.52) * mm, "mid": v(2.87, 2.96) * mm, "end": v(3.43, 2.72) * mm});
            skArc(sketch, "E19.0.4.24", {"start": v(20.5, 3.52) * mm, "mid": v(20.73, 2.96) * mm, "end": v(21.29, 2.72) * mm});
            skLineSegment(sketch, "E19.0.4.25", {"start": v(20.5, 3.52) * mm, "end": v(20.5, 15.03) * mm});
            skArc(sketch, "E19.0.4.26", {"start": v(21.29, 15.82) * mm, "mid": v(20.73, 15.59) * mm, "end": v(20.5, 15.03) * mm});
            skLineSegment(sketch, "E19.0.4.27", {"start": v(21.29, 15.82) * mm, "end": v(32.8, 15.82) * mm});
            skArc(sketch, "E19.0.4.28", {"start": v(33.6, 15.03) * mm, "mid": v(33.36, 15.59) * mm, "end": v(32.8, 15.82) * mm});
            skLineSegment(sketch, "E19.0.4.29", {"start": v(33.6, 3.52) * mm, "end": v(33.6, 15.03) * mm});
            skArc(sketch, "E19.0.4.30", {"start": v(32.8, 2.72) * mm, "mid": v(33.36, 2.96) * mm, "end": v(33.6, 3.52) * mm});
            skLineSegment(sketch, "E19.0.4.31", {"start": v(21.29, 2.72) * mm, "end": v(32.8, 2.72) * mm});
            skLineSegment(sketch, "E19.direction1", {"start": v(-33.07, -67.92) * mm, "end": v(-7.67, -67.92) * mm, "construction": true});
            skLineSegment(sketch, "E19.direction2", {"start": v(-33.07, -67.92) * mm, "end": v(-33.07, -50.06) * mm, "construction": true});
            skSolve(sketch);
        }
        {
            var Q0;
            Q0=makeQuery(id+"F6.imprint","IMPRINT",FACE,{"disambiguationData":[TD([[makeQuery(id+"F6.imprint","IMPRINT",EDGE,{"derivedFrom":sQuery(id+"F6.wireOp",EDGE,"E19.0.4.0")}),-1.0]])]});
            var Q1;
            Q1=makeQuery(id+"F6.imprint","IMPRINT",FACE,{"disambiguationData":[TD([[makeQuery(id+"F6.imprint","IMPRINT",EDGE,{"derivedFrom":sQuery(id+"F6.wireOp",EDGE,"E19.0.4.8")}),1.0]])]});
            var Q2;
            Q2=makeQuery(id+"F6.imprint","IMPRINT",FACE,{"disambiguationData":[TD([[makeQuery(id+"F6.imprint","IMPRINT",EDGE,{"derivedFrom":sQuery(id+"F6.wireOp",EDGE,"E19.0.4.16")}),-1.0]])]});
            var Q3;
            Q3=makeQuery(id+"F6.imprint","IMPRINT",FACE,{"disambiguationData":[TD([[makeQuery(id+"F6.imprint","IMPRINT",EDGE,{"derivedFrom":sQuery(id+"F6.wireOp",EDGE,"E19.0.4.24")}),1.0]])]});
            var Q4;
            Q4=makeQuery(id+"F6.imprint","IMPRINT",FACE,{"disambiguationData":[TD([[makeQuery(id+"F6.imprint","IMPRINT",EDGE,{"derivedFrom":sQuery(id+"F6.wireOp",EDGE,"E19.0.3.24")}),1.0]])]});
            var Q5;
            Q5=makeQuery(id+"F6.imprint","IMPRINT",FACE,{"disambiguationData":[TD([[makeQuery(id+"F6.imprint","IMPRINT",EDGE,{"derivedFrom":sQuery(id+"F6.wireOp",EDGE,"E19.0.3.16")}),-1.0]])]});
            var Q6;
            Q6=makeQuery(id+"F6.imprint","IMPRINT",FACE,{"disambiguationData":[TD([[makeQuery(id+"F6.imprint","IMPRINT",EDGE,{"derivedFrom":sQuery(id+"F6.wireOp",EDGE,"E19.0.3.8")}),1.0]])]});
            var Q7;
            Q7=makeQuery(id+"F6.imprint","IMPRINT",FACE,{"disambiguationData":[TD([[makeQuery(id+"F6.imprint","IMPRINT",EDGE,{"derivedFrom":sQuery(id+"F6.wireOp",EDGE,"E19.0.3.0")}),-1.0]])]});
            var Q8;
            Q8=makeQuery(id+"F6.imprint","IMPRINT",FACE,{"disambiguationData":[TD([[makeQuery(id+"F6.imprint","IMPRINT",EDGE,{"derivedFrom":sQuery(id+"F6.wireOp",EDGE,"E19.0.2.0")}),-1.0]])]});
            var Q9;
            Q9=makeQuery(id+"F6.imprint","IMPRINT",FACE,{"disambiguationData":[TD([[makeQuery(id+"F6.imprint","IMPRINT",EDGE,{"derivedFrom":sQuery(id+"F6.wireOp",EDGE,"E19.0.2.8")}),1.0]])]});
            var Q10;
            Q10=makeQuery(id+"F6.imprint","IMPRINT",FACE,{"disambiguationData":[TD([[makeQuery(id+"F6.imprint","IMPRINT",EDGE,{"derivedFrom":sQuery(id+"F6.wireOp",EDGE,"E19.0.2.16")}),-1.0]])]});
            var Q11;
            Q11=makeQuery(id+"F6.imprint","IMPRINT",FACE,{"disambiguationData":[TD([[makeQuery(id+"F6.imprint","IMPRINT",EDGE,{"derivedFrom":sQuery(id+"F6.wireOp",EDGE,"E19.0.2.24")}),1.0]])]});
            var Q12;
            Q12=makeQuery(id+"F6.imprint","IMPRINT",FACE,{"disambiguationData":[TD([[makeQuery(id+"F6.imprint","IMPRINT",EDGE,{"derivedFrom":sQuery(id+"F6.wireOp",EDGE,"E19.0.1.24")}),1.0]])]});
            var Q13;
            Q13=makeQuery(id+"F6.imprint","IMPRINT",FACE,{"disambiguationData":[TD([[makeQuery(id+"F6.imprint","IMPRINT",EDGE,{"derivedFrom":sQuery(id+"F6.wireOp",EDGE,"E19.0.1.16")}),-1.0]])]});
            var Q14;
            Q14=makeQuery(id+"F6.imprint","IMPRINT",FACE,{"disambiguationData":[TD([[makeQuery(id+"F6.imprint","IMPRINT",EDGE,{"derivedFrom":sQuery(id+"F6.wireOp",EDGE,"E19.0.1.8")}),1.0]])]});
            var Q15;
            Q15=makeQuery(id+"F6.imprint","IMPRINT",FACE,{"disambiguationData":[TD([[makeQuery(id+"F6.imprint","IMPRINT",EDGE,{"derivedFrom":sQuery(id+"F6.wireOp",EDGE,"E19.0.1.0")}),-1.0]])]});
            var Q16;
            {var subQ1=sQuery(id+"F6.wireOp",EDGE,"E17.3.0.3");Q16=makeQuery(id+"F6.imprint","IMPRINT",FACE,{"disambiguationData":[TD([[makeQuery(id+"F6.imprint","IMPRINT",EDGE,{"derivedFrom":subQ1}),1.0]])]});}
            var Q17;
            Q17=makeQuery(id+"F6.imprint","IMPRINT",FACE,{"disambiguationData":[TD([[makeQuery(id+"F6.imprint","IMPRINT",EDGE,{"derivedFrom":sQuery(id+"F6.wireOp",EDGE,"E17.2.0.0")}),-1.0]])]});
            var Q18;
            Q18=makeQuery(id+"F6.imprint","IMPRINT",FACE,{"disambiguationData":[TD([[makeQuery(id+"F6.imprint","IMPRINT",EDGE,{"derivedFrom":sQuery(id+"F6.wireOp",EDGE,"E17.1.0.0")}),-1.0]])]});
            var Q19;
            Q19=makeQuery(id+"F6.imprint","IMPRINT",FACE,{"disambiguationData":[TD([[makeQuery(id+"F6.imprint","IMPRINT",EDGE,{"derivedFrom":sQuery(id+"F6.wireOp",EDGE,"E10.top")}),-1.0]])]});
            var Q20;
            Q20=makeQuery(id+"F6.imprint","IMPRINT",FACE,{"disambiguationData":[TD([[makeQuery(id+"F6.imprint","IMPRINT",EDGE,{"derivedFrom":sQuery(id+"F6.wireOp",EDGE,"E17.3.0.0")}),-1.0]])]});
            var Q21;
            {var subQ0=sQuery(id+"F6.wireOp",EDGE,"E14.filletArc");Q21=makeQuery(id+"F6.imprint","IMPRINT",FACE,{"disambiguationData":[TD([[makeQuery(id+"F6.imprint","IMPRINT",EDGE,{"derivedFrom":subQ0}),1.0]])]});}
            var Q22;
            {var subQ0=sQuery(id+"F6.wireOp",EDGE,"E13.filletArc");Q22=makeQuery(id+"F6.imprint","IMPRINT",FACE,{"disambiguationData":[TD([[makeQuery(id+"F6.imprint","IMPRINT",EDGE,{"derivedFrom":subQ0}),1.0]])]});}
            extrude(context, id + "F7", {"entities" : qUnion([Q0, Q1, Q2, Q3, Q4, Q5, Q6, Q7, Q8, Q9, Q10, Q11, Q12, Q13, Q14, Q15, Q16, Q17, Q18, Q19, Q20, Q21, Q22]), "operationType" : NewBodyOperationType.REMOVE, "oppositeDirection" : true, "depth" : 25.4 * mm});
        }
        {
            var Q0;
            Q0=makeQuery(id+"F5.boolean.opBoolean","COPY",FACE,{"derivedFrom":makeQuery(id+"F5.opExtrude","CAP_FACE",FACE,{"disambiguationData":[OSD([sQuery(id+"F4.wireOp",EDGE,"E2.bottom"),sQuery(id+"F4.wireOp",EDGE,"E2.top"),sQuery(id+"F4.wireOp",EDGE,"E2.left"),sQuery(id+"F4.wireOp",EDGE,"E2.right")])],"isStart":false})});
            var sketch = newSketch(context, id + "F8", { "sketchPlane" : qUnion([Q0])});
            skLineSegment(sketch, "E20.0.0", {"start": v(34.6, 71.44) * mm, "end": v(-36.99, 71.44) * mm});
            skLineSegment(sketch, "E20.0.1", {"start": v(-36.99, 71.44) * mm, "end": v(-36.99, -71.44) * mm});
            skLineSegment(sketch, "E20.0.2", {"start": v(-36.99, -71.44) * mm, "end": v(34.6, -71.44) * mm});
            skLineSegment(sketch, "E20.0.3", {"start": v(34.6, -71.44) * mm, "end": v(34.6, 71.44) * mm});
            skLineSegment(sketch, "E21.bottom", {"start": v(-33.87, -1.14) * mm, "end": v(-19.18, -1.14) * mm});
            skLineSegment(sketch, "E21.top", {"start": v(-33.87, -17.4) * mm, "end": v(-19.18, -17.4) * mm});
            skLineSegment(sketch, "E21.left", {"start": v(-34.66, -1.93) * mm, "end": v(-34.66, -16.61) * mm});
            skLineSegment(sketch, "E21.right", {"start": v(-18.39, -1.93) * mm, "end": v(-18.39, -16.61) * mm});
            skLineSegment(sketch, "E22.bottom", {"start": v(-16, -1.14) * mm, "end": v(-1.33, -1.14) * mm});
            skLineSegment(sketch, "E22.top", {"start": v(-16, -17.4) * mm, "end": v(-1.33, -17.4) * mm});
            skLineSegment(sketch, "E22.left", {"start": v(-16.8, -1.93) * mm, "end": v(-16.8, -16.61) * mm});
            skLineSegment(sketch, "E22.right", {"start": v(-0.53, -1.93) * mm, "end": v(-0.53, -16.61) * mm});
            skPoint(sketch, "E23.visualSharp", {"position": v(-34.66, -1.14) * mm});
            skArc(sketch, "E23.filletArc", {"start": v(-33.87, -1.14) * mm, "mid": v(-34.43, -1.37) * mm, "end": v(-34.66, -1.93) * mm});
            skPoint(sketch, "E24.visualSharp", {"position": v(-18.39, -1.14) * mm});
            skArc(sketch, "E24.filletArc", {"start": v(-18.39, -1.93) * mm, "mid": v(-18.62, -1.37) * mm, "end": v(-19.18, -1.14) * mm});
            skPoint(sketch, "E25.visualSharp", {"position": v(-34.66, -17.4) * mm});
            skArc(sketch, "E25.filletArc", {"start": v(-34.66, -16.61) * mm, "mid": v(-34.43, -17.17) * mm, "end": v(-33.87, -17.4) * mm});
            skPoint(sketch, "E26.visualSharp", {"position": v(-18.39, -17.4) * mm});
            skArc(sketch, "E26.filletArc", {"start": v(-19.18, -17.4) * mm, "mid": v(-18.62, -17.17) * mm, "end": v(-18.39, -16.61) * mm});
            skLineSegment(sketch, "E27", {"start": v(1.85, -17.4) * mm, "end": v(16.53, -17.4) * mm});
            skLineSegment(sketch, "E28", {"start": v(-34.66, 1.25) * mm, "end": v(-34.66, 15.93) * mm});
            skLineSegment(sketch, "E29", {"start": v(-33.87, 0.45) * mm, "end": v(-19.18, 0.45) * mm});
            skLineSegment(sketch, "E30", {"start": v(1.05, -1.93) * mm, "end": v(1.05, -16.61) * mm});
            skLineSegment(sketch, "E31", {"start": v(17.32, -1.93) * mm, "end": v(17.32, -16.61) * mm});
            skLineSegment(sketch, "E32", {"start": v(18.9, -16.61) * mm, "end": v(18.9, -1.93) * mm});
            skLineSegment(sketch, "E33", {"start": v(35.18, -1.93) * mm, "end": v(35.18, -16.61) * mm});
            skLineSegment(sketch, "E34", {"start": v(-33.87, 16.72) * mm, "end": v(-19.18, 16.72) * mm});
            skLineSegment(sketch, "E35", {"start": v(-33.87, 18.31) * mm, "end": v(-19.18, 18.31) * mm});
            skLineSegment(sketch, "E36", {"start": v(35.18, 36.17) * mm, "end": v(19.7, 36.17) * mm});
            skLineSegment(sketch, "E37", {"start": v(-33.87, 52.44) * mm, "end": v(-19.18, 52.44) * mm});
            skLineSegment(sketch, "E38", {"start": v(34.39, 54.03) * mm, "end": v(19.7, 54.03) * mm});
            skLineSegment(sketch, "E39", {"start": v(35.18, 1.25) * mm, "end": v(35.18, 15.93) * mm});
            skLineSegment(sketch, "E40", {"start": v(18.9, 1.25) * mm, "end": v(18.9, 15.93) * mm});
            skLineSegment(sketch, "E41", {"start": v(17.32, 1.25) * mm, "end": v(17.32, 15.93) * mm});
            skLineSegment(sketch, "E42", {"start": v(1.05, 1.25) * mm, "end": v(1.05, 15.93) * mm});
            skLineSegment(sketch, "E43", {"start": v(-0.53, 1.25) * mm, "end": v(-0.53, 15.93) * mm});
            skLineSegment(sketch, "E44.trimOffspring", {"start": v(1.85, 70.3) * mm, "end": v(16.53, 70.3) * mm});
            skLineSegment(sketch, "E45", {"start": v(-16.8, 1.25) * mm, "end": v(-16.8, 15.93) * mm});
            skLineSegment(sketch, "E46", {"start": v(-18.39, -1.93) * mm, "end": v(-18.39, -1.14) * mm});
            skLineSegment(sketch, "E47", {"start": v(-1.33, 70.3) * mm, "end": v(-16, 70.3) * mm});
            skLineSegment(sketch, "E48.trimOffspring", {"start": v(-19.18, 70.3) * mm, "end": v(-33.87, 70.3) * mm});
            skLineSegment(sketch, "E49.trimOffspring", {"start": v(19.7, 70.3) * mm, "end": v(34.39, 70.3) * mm});
            skLineSegment(sketch, "E50.trimOffspring", {"start": v(35.18, 54.82) * mm, "end": v(35.18, 69.5) * mm});
            skLineSegment(sketch, "E51.trimOffspring", {"start": v(18.9, 54.82) * mm, "end": v(18.9, 69.5) * mm});
            skLineSegment(sketch, "E52.trimOffspring", {"start": v(17.32, 54.82) * mm, "end": v(17.32, 69.5) * mm});
            skLineSegment(sketch, "E53.trimOffspring", {"start": v(16.53, 54.03) * mm, "end": v(1.85, 54.03) * mm});
            skLineSegment(sketch, "E54.trimOffspring", {"start": v(19.7, 52.44) * mm, "end": v(34.39, 52.44) * mm});
            skLineSegment(sketch, "E55.trimOffspring", {"start": v(-1.33, 54.03) * mm, "end": v(-16, 54.03) * mm});
            skLineSegment(sketch, "E56.trimOffspring", {"start": v(1.85, 52.44) * mm, "end": v(16.53, 52.44) * mm});
            skLineSegment(sketch, "E57.trimOffspring", {"start": v(1.05, 54.82) * mm, "end": v(1.05, 69.5) * mm});
            skLineSegment(sketch, "E58.trimOffspring", {"start": v(-0.53, 54.82) * mm, "end": v(-0.53, 69.5) * mm});
            skLineSegment(sketch, "E59.trimOffspring", {"start": v(-16.8, 54.82) * mm, "end": v(-16.8, 69.5) * mm});
            skLineSegment(sketch, "E60.trimOffspring", {"start": v(-19.18, 54.03) * mm, "end": v(-33.87, 54.03) * mm});
            skLineSegment(sketch, "E61.trimOffspring", {"start": v(-18.39, 54.82) * mm, "end": v(-18.39, 69.5) * mm});
            skLineSegment(sketch, "E62.trimOffspring", {"start": v(-16, 52.44) * mm, "end": v(-1.33, 52.44) * mm});
            skLineSegment(sketch, "E63.trimOffspring", {"start": v(-34.66, 54.82) * mm, "end": v(-34.66, 69.5) * mm});
            skLineSegment(sketch, "E64.trimOffspring", {"start": v(-34.66, 36.96) * mm, "end": v(-34.66, 51.65) * mm});
            skLineSegment(sketch, "E65.trimOffspring", {"start": v(-18.39, 36.96) * mm, "end": v(-18.39, 51.65) * mm});
            skLineSegment(sketch, "E66.trimOffspring", {"start": v(-19.18, 36.17) * mm, "end": v(-33.87, 36.17) * mm});
            skLineSegment(sketch, "E67.trimOffspring", {"start": v(-16.8, 36.96) * mm, "end": v(-16.8, 51.65) * mm});
            skLineSegment(sketch, "E68.trimOffspring", {"start": v(-16, 34.58) * mm, "end": v(-1.33, 34.58) * mm});
            skLineSegment(sketch, "E69.trimOffspring", {"start": v(-0.53, 36.96) * mm, "end": v(-0.53, 51.65) * mm});
            skLineSegment(sketch, "E70.trimOffspring", {"start": v(-1.33, 36.17) * mm, "end": v(-16, 36.17) * mm});
            skLineSegment(sketch, "E71.trimOffspring", {"start": v(1.05, 36.96) * mm, "end": v(1.05, 51.65) * mm});
            skLineSegment(sketch, "E72.trimOffspring", {"start": v(1.85, 34.58) * mm, "end": v(16.53, 34.58) * mm});
            skLineSegment(sketch, "E73.trimOffspring", {"start": v(17.32, 36.96) * mm, "end": v(17.32, 51.65) * mm});
            skLineSegment(sketch, "E74.trimOffspring", {"start": v(18.9, 36.96) * mm, "end": v(18.9, 51.65) * mm});
            skLineSegment(sketch, "E75.trimOffspring", {"start": v(16.53, 36.17) * mm, "end": v(1.85, 36.17) * mm});
            skLineSegment(sketch, "E76.trimOffspring", {"start": v(19.7, 34.58) * mm, "end": v(34.39, 34.58) * mm});
            skLineSegment(sketch, "E77.trimOffspring", {"start": v(35.18, 36.17) * mm, "end": v(35.18, 51.65) * mm});
            skLineSegment(sketch, "E78", {"start": v(-33.87, 34.58) * mm, "end": v(-19.18, 34.58) * mm});
            skLineSegment(sketch, "E79.trimOffspring", {"start": v(-34.66, 19.1) * mm, "end": v(-34.66, 33.79) * mm});
            skLineSegment(sketch, "E80.trimOffspring", {"start": v(-18.39, 19.1) * mm, "end": v(-18.39, 33.79) * mm});
            skLineSegment(sketch, "E81.trimOffspring", {"start": v(-16, 18.31) * mm, "end": v(-1.33, 18.31) * mm});
            skLineSegment(sketch, "E82.trimOffspring", {"start": v(-16.8, 19.1) * mm, "end": v(-16.8, 33.79) * mm});
            skLineSegment(sketch, "E83.trimOffspring", {"start": v(-16, 16.72) * mm, "end": v(-1.33, 16.72) * mm});
            skLineSegment(sketch, "E84.trimOffspring", {"start": v(-0.53, 19.1) * mm, "end": v(-0.53, 33.79) * mm});
            skLineSegment(sketch, "E85.trimOffspring", {"start": v(1.85, 18.31) * mm, "end": v(16.53, 18.31) * mm});
            skLineSegment(sketch, "E86.trimOffspring", {"start": v(1.05, 19.1) * mm, "end": v(1.05, 33.79) * mm});
            skLineSegment(sketch, "E87.trimOffspring", {"start": v(1.85, 16.72) * mm, "end": v(16.53, 16.72) * mm});
            skLineSegment(sketch, "E88.trimOffspring", {"start": v(17.32, 19.1) * mm, "end": v(17.32, 33.79) * mm});
            skLineSegment(sketch, "E89.trimOffspring", {"start": v(19.7, 18.31) * mm, "end": v(34.39, 18.31) * mm});
            skLineSegment(sketch, "E90.trimOffspring", {"start": v(18.9, 19.1) * mm, "end": v(18.9, 33.79) * mm});
            skLineSegment(sketch, "E91.trimOffspring", {"start": v(19.7, 16.72) * mm, "end": v(34.39, 16.72) * mm});
            skLineSegment(sketch, "E92.trimOffspring", {"start": v(35.18, 19.1) * mm, "end": v(35.18, 33.79) * mm});
            skLineSegment(sketch, "E93.trimOffspring", {"start": v(19.7, 0.45) * mm, "end": v(34.39, 0.45) * mm});
            skLineSegment(sketch, "E94.trimOffspring", {"start": v(19.7, -1.14) * mm, "end": v(34.39, -1.14) * mm});
            skLineSegment(sketch, "E95.trimOffspring", {"start": v(1.85, 0.45) * mm, "end": v(16.53, 0.45) * mm});
            skLineSegment(sketch, "E96", {"start": v(1.85, -1.14) * mm, "end": v(16.53, -1.14) * mm});
            skLineSegment(sketch, "E97.trimOffspring", {"start": v(-18.39, 1.25) * mm, "end": v(-18.39, 15.93) * mm});
            skLineSegment(sketch, "E98.trimOffspring", {"start": v(-16, 0.45) * mm, "end": v(-1.33, 0.45) * mm});
            skPoint(sketch, "E99.visualSharp", {"position": v(-16.8, -1.14) * mm});
            skArc(sketch, "E99.filletArc", {"start": v(-16, -1.14) * mm, "mid": v(-16.57, -1.37) * mm, "end": v(-16.8, -1.93) * mm});
            skPoint(sketch, "E100.visualSharp", {"position": v(-0.53, -1.14) * mm});
            skArc(sketch, "E100.filletArc", {"start": v(-0.53, -1.93) * mm, "mid": v(-0.76, -1.37) * mm, "end": v(-1.33, -1.14) * mm});
            skPoint(sketch, "E101.visualSharp", {"position": v(-0.53, -17.4) * mm});
            skArc(sketch, "E101.filletArc", {"start": v(-1.33, -17.4) * mm, "mid": v(-0.76, -17.17) * mm, "end": v(-0.53, -16.61) * mm});
            skPoint(sketch, "E102.visualSharp", {"position": v(-16.8, -17.4) * mm});
            skArc(sketch, "E102.filletArc", {"start": v(-16.8, -16.61) * mm, "mid": v(-16.57, -17.17) * mm, "end": v(-16, -17.4) * mm});
            skPoint(sketch, "E103.visualSharp", {"position": v(1.05, -1.14) * mm});
            skArc(sketch, "E103.filletArc", {"start": v(1.85, -1.14) * mm, "mid": v(1.28, -1.37) * mm, "end": v(1.05, -1.93) * mm});
            skPoint(sketch, "E104.visualSharp", {"position": v(17.32, -1.14) * mm});
            skArc(sketch, "E104.filletArc", {"start": v(17.32, -1.93) * mm, "mid": v(17.1, -1.37) * mm, "end": v(16.53, -1.14) * mm});
            skArc(sketch, "E105.filletArc", {"start": v(16.53, -17.4) * mm, "mid": v(17.1, -17.17) * mm, "end": v(17.32, -16.61) * mm});
            skArc(sketch, "E106.filletArc", {"start": v(1.05, -16.61) * mm, "mid": v(1.28, -17.17) * mm, "end": v(1.85, -17.4) * mm});
            skLineSegment(sketch, "E107", {"start": v(19.7, -17.4) * mm, "end": v(34.39, -17.4) * mm});
            skPoint(sketch, "E108.visualSharp", {"position": v(18.9, -1.14) * mm});
            skArc(sketch, "E108.filletArc", {"start": v(19.7, -1.14) * mm, "mid": v(19.14, -1.37) * mm, "end": v(18.9, -1.93) * mm});
            skPoint(sketch, "E109.visualSharp", {"position": v(35.18, -1.14) * mm});
            skArc(sketch, "E109.filletArc", {"start": v(35.18, -1.93) * mm, "mid": v(34.95, -1.37) * mm, "end": v(34.39, -1.14) * mm});
            skPoint(sketch, "E110.visualSharp", {"position": v(35.18, -17.4) * mm});
            skArc(sketch, "E110.filletArc", {"start": v(34.39, -17.4) * mm, "mid": v(34.95, -17.17) * mm, "end": v(35.18, -16.61) * mm});
            skPoint(sketch, "E111.visualSharp", {"position": v(18.9, -17.4) * mm});
            skArc(sketch, "E111.filletArc", {"start": v(18.9, -16.61) * mm, "mid": v(19.14, -17.17) * mm, "end": v(19.7, -17.4) * mm});
            skPoint(sketch, "E112.visualSharp", {"position": v(18.9, 16.72) * mm});
            skArc(sketch, "E112.filletArc", {"start": v(19.7, 16.72) * mm, "mid": v(19.14, 16.5) * mm, "end": v(18.9, 15.93) * mm});
            skPoint(sketch, "E113.visualSharp", {"position": v(35.18, 16.72) * mm});
            skArc(sketch, "E113.filletArc", {"start": v(35.18, 15.93) * mm, "mid": v(34.95, 16.5) * mm, "end": v(34.39, 16.72) * mm});
            skPoint(sketch, "E114.visualSharp", {"position": v(35.18, 0.45) * mm});
            skArc(sketch, "E114.filletArc", {"start": v(34.39, 0.45) * mm, "mid": v(34.95, 0.68) * mm, "end": v(35.18, 1.25) * mm});
            skPoint(sketch, "E115.visualSharp", {"position": v(18.9, 0.45) * mm});
            skArc(sketch, "E115.filletArc", {"start": v(18.9, 1.25) * mm, "mid": v(19.14, 0.68) * mm, "end": v(19.7, 0.45) * mm});
            skPoint(sketch, "E116.visualSharp", {"position": v(17.32, 0.45) * mm});
            skArc(sketch, "E116.filletArc", {"start": v(16.53, 0.45) * mm, "mid": v(17.1, 0.68) * mm, "end": v(17.32, 1.25) * mm});
            skPoint(sketch, "E117.visualSharp", {"position": v(17.32, 16.72) * mm});
            skArc(sketch, "E117.filletArc", {"start": v(17.32, 15.93) * mm, "mid": v(17.1, 16.5) * mm, "end": v(16.53, 16.72) * mm});
            skPoint(sketch, "E118.visualSharp", {"position": v(1.05, 16.72) * mm});
            skArc(sketch, "E118.filletArc", {"start": v(1.85, 16.72) * mm, "mid": v(1.28, 16.5) * mm, "end": v(1.05, 15.93) * mm});
            skPoint(sketch, "E119.visualSharp", {"position": v(1.05, 0.45) * mm});
            skArc(sketch, "E119.filletArc", {"start": v(1.05, 1.25) * mm, "mid": v(1.28, 0.68) * mm, "end": v(1.85, 0.45) * mm});
            skPoint(sketch, "E120.visualSharp", {"position": v(-0.53, 0.45) * mm});
            skArc(sketch, "E120.filletArc", {"start": v(-1.33, 0.45) * mm, "mid": v(-0.76, 0.68) * mm, "end": v(-0.53, 1.25) * mm});
            skPoint(sketch, "E121.visualSharp", {"position": v(-0.53, 16.72) * mm});
            skArc(sketch, "E121.filletArc", {"start": v(-0.53, 15.93) * mm, "mid": v(-0.76, 16.5) * mm, "end": v(-1.33, 16.72) * mm});
            skPoint(sketch, "E122.visualSharp", {"position": v(-16.8, 16.72) * mm});
            skArc(sketch, "E122.filletArc", {"start": v(-16, 16.72) * mm, "mid": v(-16.57, 16.5) * mm, "end": v(-16.8, 15.93) * mm});
            skPoint(sketch, "E123.visualSharp", {"position": v(-16.8, 0.45) * mm});
            skArc(sketch, "E123.filletArc", {"start": v(-16.8, 1.25) * mm, "mid": v(-16.57, 0.68) * mm, "end": v(-16, 0.45) * mm});
            skPoint(sketch, "E124.visualSharp", {"position": v(-18.39, 16.72) * mm});
            skArc(sketch, "E124.filletArc", {"start": v(-18.39, 15.93) * mm, "mid": v(-18.62, 16.5) * mm, "end": v(-19.18, 16.72) * mm});
            skPoint(sketch, "E125.visualSharp", {"position": v(-18.39, 0.45) * mm});
            skArc(sketch, "E125.filletArc", {"start": v(-19.18, 0.45) * mm, "mid": v(-18.62, 0.68) * mm, "end": v(-18.39, 1.25) * mm});
            skPoint(sketch, "E126.newPointB", {"position": v(-34.66, 0.45) * mm});
            skArc(sketch, "E126.filletArc", {"start": v(-34.66, 1.25) * mm, "mid": v(-34.43, 0.68) * mm, "end": v(-33.87, 0.45) * mm});
            skPoint(sketch, "E127.visualSharp", {"position": v(-34.66, 16.72) * mm});
            skArc(sketch, "E127.filletArc", {"start": v(-33.87, 16.72) * mm, "mid": v(-34.43, 16.5) * mm, "end": v(-34.66, 15.93) * mm});
            skPoint(sketch, "E128.visualSharp", {"position": v(-18.39, 18.31) * mm});
            skArc(sketch, "E128.filletArc", {"start": v(-19.18, 18.31) * mm, "mid": v(-18.62, 18.54) * mm, "end": v(-18.39, 19.1) * mm});
            skPoint(sketch, "E129.visualSharp", {"position": v(-18.39, 34.58) * mm});
            skArc(sketch, "E129.filletArc", {"start": v(-18.39, 33.79) * mm, "mid": v(-18.62, 34.35) * mm, "end": v(-19.18, 34.58) * mm});
            skPoint(sketch, "E130.visualSharp", {"position": v(-34.66, 34.58) * mm});
            skArc(sketch, "E130.filletArc", {"start": v(-33.87, 34.58) * mm, "mid": v(-34.43, 34.35) * mm, "end": v(-34.66, 33.79) * mm});
            skPoint(sketch, "E131.visualSharp", {"position": v(-34.66, 18.31) * mm});
            skArc(sketch, "E131.filletArc", {"start": v(-34.66, 19.1) * mm, "mid": v(-34.43, 18.54) * mm, "end": v(-33.87, 18.31) * mm});
            skPoint(sketch, "E132.visualSharp", {"position": v(-16.8, 34.58) * mm});
            skArc(sketch, "E132.filletArc", {"start": v(-16, 34.58) * mm, "mid": v(-16.57, 34.35) * mm, "end": v(-16.8, 33.79) * mm});
            skPoint(sketch, "E133.visualSharp", {"position": v(-0.53, 34.58) * mm});
            skArc(sketch, "E133.filletArc", {"start": v(-0.53, 33.79) * mm, "mid": v(-0.76, 34.35) * mm, "end": v(-1.33, 34.58) * mm});
            skPoint(sketch, "E134.visualSharp", {"position": v(-0.53, 18.31) * mm});
            skArc(sketch, "E134.filletArc", {"start": v(-1.33, 18.31) * mm, "mid": v(-0.76, 18.54) * mm, "end": v(-0.53, 19.1) * mm});
            skPoint(sketch, "E135.visualSharp", {"position": v(-16.8, 18.31) * mm});
            skArc(sketch, "E135.filletArc", {"start": v(-16.8, 19.1) * mm, "mid": v(-16.57, 18.54) * mm, "end": v(-16, 18.31) * mm});
            skPoint(sketch, "E136.visualSharp", {"position": v(1.05, 34.58) * mm});
            skArc(sketch, "E136.filletArc", {"start": v(1.85, 34.58) * mm, "mid": v(1.28, 34.35) * mm, "end": v(1.05, 33.79) * mm});
            skPoint(sketch, "E137.visualSharp", {"position": v(17.32, 34.58) * mm});
            skArc(sketch, "E137.filletArc", {"start": v(17.32, 33.79) * mm, "mid": v(17.1, 34.35) * mm, "end": v(16.53, 34.58) * mm});
            skPoint(sketch, "E138.visualSharp", {"position": v(17.32, 18.31) * mm});
            skArc(sketch, "E138.filletArc", {"start": v(16.53, 18.31) * mm, "mid": v(17.1, 18.54) * mm, "end": v(17.32, 19.1) * mm});
            skPoint(sketch, "E139.visualSharp", {"position": v(1.05, 18.31) * mm});
            skArc(sketch, "E139.filletArc", {"start": v(1.05, 19.1) * mm, "mid": v(1.28, 18.54) * mm, "end": v(1.85, 18.31) * mm});
            skPoint(sketch, "E140.visualSharp", {"position": v(18.9, 34.58) * mm});
            skArc(sketch, "E140.filletArc", {"start": v(19.7, 34.58) * mm, "mid": v(19.14, 34.35) * mm, "end": v(18.9, 33.79) * mm});
            skPoint(sketch, "E141.visualSharp", {"position": v(35.18, 34.58) * mm});
            skArc(sketch, "E141.filletArc", {"start": v(35.18, 33.79) * mm, "mid": v(34.95, 34.35) * mm, "end": v(34.39, 34.58) * mm});
            skPoint(sketch, "E142.visualSharp", {"position": v(18.9, 18.31) * mm});
            skArc(sketch, "E142.filletArc", {"start": v(18.9, 19.1) * mm, "mid": v(19.14, 18.54) * mm, "end": v(19.7, 18.31) * mm});
            skPoint(sketch, "E143.visualSharp", {"position": v(35.18, 18.31) * mm});
            skArc(sketch, "E143.filletArc", {"start": v(34.39, 18.31) * mm, "mid": v(34.95, 18.54) * mm, "end": v(35.18, 19.1) * mm});
            skPoint(sketch, "E144.visualSharp", {"position": v(35.18, 52.44) * mm});
            skArc(sketch, "E144.filletArc", {"start": v(35.18, 51.65) * mm, "mid": v(34.95, 52.21) * mm, "end": v(34.39, 52.44) * mm});
            skPoint(sketch, "E145.visualSharp", {"position": v(18.9, 52.44) * mm});
            skArc(sketch, "E145.filletArc", {"start": v(19.7, 52.44) * mm, "mid": v(19.14, 52.21) * mm, "end": v(18.9, 51.65) * mm});
            skPoint(sketch, "E146.visualSharp", {"position": v(18.9, 36.17) * mm});
            skArc(sketch, "E146.filletArc", {"start": v(18.9, 36.96) * mm, "mid": v(19.14, 36.4) * mm, "end": v(19.7, 36.17) * mm});
            skPoint(sketch, "E147.visualSharp", {"position": v(17.32, 36.17) * mm});
            skArc(sketch, "E147.filletArc", {"start": v(16.53, 36.17) * mm, "mid": v(17.1, 36.4) * mm, "end": v(17.32, 36.96) * mm});
            skPoint(sketch, "E148.visualSharp", {"position": v(1.05, 52.44) * mm});
            skArc(sketch, "E148.filletArc", {"start": v(1.85, 52.44) * mm, "mid": v(1.28, 52.21) * mm, "end": v(1.05, 51.65) * mm});
            skPoint(sketch, "E149.visualSharp", {"position": v(17.32, 52.44) * mm});
            skArc(sketch, "E149.filletArc", {"start": v(17.32, 51.65) * mm, "mid": v(17.1, 52.21) * mm, "end": v(16.53, 52.44) * mm});
            skPoint(sketch, "E150.visualSharp", {"position": v(1.05, 36.17) * mm});
            skArc(sketch, "E150.filletArc", {"start": v(1.05, 36.96) * mm, "mid": v(1.28, 36.4) * mm, "end": v(1.85, 36.17) * mm});
            skPoint(sketch, "E151.visualSharp", {"position": v(-0.53, 52.44) * mm});
            skArc(sketch, "E151.filletArc", {"start": v(-0.53, 51.65) * mm, "mid": v(-0.76, 52.21) * mm, "end": v(-1.33, 52.44) * mm});
            skPoint(sketch, "E152.visualSharp", {"position": v(-0.53, 36.17) * mm});
            skArc(sketch, "E152.filletArc", {"start": v(-1.33, 36.17) * mm, "mid": v(-0.76, 36.4) * mm, "end": v(-0.53, 36.96) * mm});
            skPoint(sketch, "E153.visualSharp", {"position": v(-16.8, 36.17) * mm});
            skArc(sketch, "E153.filletArc", {"start": v(-16.8, 36.96) * mm, "mid": v(-16.57, 36.4) * mm, "end": v(-16, 36.17) * mm});
            skPoint(sketch, "E154.visualSharp", {"position": v(-16.8, 52.44) * mm});
            skArc(sketch, "E154.filletArc", {"start": v(-16, 52.44) * mm, "mid": v(-16.57, 52.21) * mm, "end": v(-16.8, 51.65) * mm});
            skPoint(sketch, "E155.visualSharp", {"position": v(-18.39, 36.17) * mm});
            skArc(sketch, "E155.filletArc", {"start": v(-19.18, 36.17) * mm, "mid": v(-18.62, 36.4) * mm, "end": v(-18.39, 36.96) * mm});
            skPoint(sketch, "E156.visualSharp", {"position": v(-18.39, 52.44) * mm});
            skArc(sketch, "E156.filletArc", {"start": v(-18.39, 51.65) * mm, "mid": v(-18.62, 52.21) * mm, "end": v(-19.18, 52.44) * mm});
            skPoint(sketch, "E157.visualSharp", {"position": v(-34.66, 52.44) * mm});
            skArc(sketch, "E157.filletArc", {"start": v(-33.87, 52.44) * mm, "mid": v(-34.43, 52.21) * mm, "end": v(-34.66, 51.65) * mm});
            skPoint(sketch, "E158.visualSharp", {"position": v(-34.66, 36.17) * mm});
            skArc(sketch, "E158.filletArc", {"start": v(-34.66, 36.96) * mm, "mid": v(-34.43, 36.4) * mm, "end": v(-33.87, 36.17) * mm});
            skPoint(sketch, "E159.visualSharp", {"position": v(-18.39, 70.3) * mm});
            skArc(sketch, "E159.filletArc", {"start": v(-18.39, 69.5) * mm, "mid": v(-18.62, 70.07) * mm, "end": v(-19.18, 70.3) * mm});
            skPoint(sketch, "E160.visualSharp", {"position": v(-34.66, 54.03) * mm});
            skArc(sketch, "E160.filletArc", {"start": v(-34.66, 54.82) * mm, "mid": v(-34.43, 54.26) * mm, "end": v(-33.87, 54.03) * mm});
            skPoint(sketch, "E161.visualSharp", {"position": v(-18.39, 54.03) * mm});
            skArc(sketch, "E161.filletArc", {"start": v(-19.18, 54.03) * mm, "mid": v(-18.62, 54.26) * mm, "end": v(-18.39, 54.82) * mm});
            skPoint(sketch, "E162.visualSharp", {"position": v(-34.66, 70.3) * mm});
            skArc(sketch, "E162.filletArc", {"start": v(-33.87, 70.3) * mm, "mid": v(-34.43, 70.07) * mm, "end": v(-34.66, 69.5) * mm});
            skPoint(sketch, "E163.visualSharp", {"position": v(-16.8, 70.3) * mm});
            skArc(sketch, "E163.filletArc", {"start": v(-16, 70.3) * mm, "mid": v(-16.57, 70.07) * mm, "end": v(-16.8, 69.5) * mm});
            skPoint(sketch, "E164.visualSharp", {"position": v(-0.53, 54.03) * mm});
            skArc(sketch, "E164.filletArc", {"start": v(-1.33, 54.03) * mm, "mid": v(-0.76, 54.26) * mm, "end": v(-0.53, 54.82) * mm});
            skPoint(sketch, "E165.visualSharp", {"position": v(-16.8, 54.03) * mm});
            skArc(sketch, "E165.filletArc", {"start": v(-16.8, 54.82) * mm, "mid": v(-16.57, 54.26) * mm, "end": v(-16, 54.03) * mm});
            skPoint(sketch, "E166.visualSharp", {"position": v(-0.53, 70.3) * mm});
            skArc(sketch, "E166.filletArc", {"start": v(-0.53, 69.5) * mm, "mid": v(-0.76, 70.07) * mm, "end": v(-1.33, 70.3) * mm});
            skPoint(sketch, "E167.visualSharp", {"position": v(1.05, 70.3) * mm});
            skArc(sketch, "E167.filletArc", {"start": v(1.85, 70.3) * mm, "mid": v(1.28, 70.07) * mm, "end": v(1.05, 69.5) * mm});
            skPoint(sketch, "E168.visualSharp", {"position": v(17.32, 70.3) * mm});
            skArc(sketch, "E168.filletArc", {"start": v(17.32, 69.5) * mm, "mid": v(17.1, 70.07) * mm, "end": v(16.53, 70.3) * mm});
            skPoint(sketch, "E169.visualSharp", {"position": v(17.32, 54.03) * mm});
            skArc(sketch, "E169.filletArc", {"start": v(16.53, 54.03) * mm, "mid": v(17.1, 54.26) * mm, "end": v(17.32, 54.82) * mm});
            skPoint(sketch, "E170.visualSharp", {"position": v(1.05, 54.03) * mm});
            skArc(sketch, "E170.filletArc", {"start": v(1.05, 54.82) * mm, "mid": v(1.28, 54.26) * mm, "end": v(1.85, 54.03) * mm});
            skPoint(sketch, "E171.visualSharp", {"position": v(18.9, 54.03) * mm});
            skArc(sketch, "E171.filletArc", {"start": v(18.9, 54.82) * mm, "mid": v(19.14, 54.26) * mm, "end": v(19.7, 54.03) * mm});
            skPoint(sketch, "E172.visualSharp", {"position": v(35.18, 54.03) * mm});
            skArc(sketch, "E172.filletArc", {"start": v(34.39, 54.03) * mm, "mid": v(34.95, 54.26) * mm, "end": v(35.18, 54.82) * mm});
            skPoint(sketch, "E173.visualSharp", {"position": v(35.18, 70.3) * mm});
            skArc(sketch, "E173.filletArc", {"start": v(35.18, 69.5) * mm, "mid": v(34.95, 70.07) * mm, "end": v(34.39, 70.3) * mm});
            skPoint(sketch, "E174.visualSharp", {"position": v(18.9, 70.3) * mm});
            skArc(sketch, "E174.filletArc", {"start": v(19.7, 70.3) * mm, "mid": v(19.14, 70.07) * mm, "end": v(18.9, 69.5) * mm});
            skSolve(sketch);
        }
        {
            var Q0;
            Q0 = qSketchRegion(id + "F8", true);
            var Q1;
            Q1=makeQuery(id+"F1.opExtrude","CAP_FACE",FACE,{"disambiguationData":[OSD([sQuery(id+"F0.wireOp",EDGE,"E0.bottom"),sQuery(id+"F0.wireOp",EDGE,"E0.top"),sQuery(id+"F0.wireOp",EDGE,"E0.left"),sQuery(id+"F0.wireOp",EDGE,"E0.right")])],"isStart":true});
            extrude(context, id + "F9", {"entities" : qUnion([Q0, Q1]), "operationType" : NewBodyOperationType.REMOVE, "depth" : 25.4 * mm});
        }
        {
            var Q0;
            Q0=makeQuery(id+"F5.boolean.opBoolean","COPY",FACE,{"derivedFrom":makeQuery(id+"F5.opExtrude","CAP_FACE",FACE,{"disambiguationData":[OSD([sQuery(id+"F4.wireOp",EDGE,"E2.bottom"),sQuery(id+"F4.wireOp",EDGE,"E2.top"),sQuery(id+"F4.wireOp",EDGE,"E2.left"),sQuery(id+"F4.wireOp",EDGE,"E2.right")])],"isStart":false})});
            var sketch = newSketch(context, id + "F10", { "sketchPlane" : qUnion([Q0])});
            skLineSegment(sketch, "E175", {"start": v(-36.99, -20.96) * mm, "end": v(34.6, -20.96) * mm});
            skArc(sketch, "E176.0.0", {"start": v(34.6, 18.34) * mm, "mid": v(34.5, 18.32) * mm, "end": v(34.39, 18.31) * mm});
            skLineSegment(sketch, "E176.0.1", {"start": v(34.39, 18.31) * mm, "end": v(19.7, 18.31) * mm});
            skArc(sketch, "E176.0.2", {"start": v(19.7, 18.31) * mm, "mid": v(19.14, 18.54) * mm, "end": v(18.9, 19.1) * mm});
            skLineSegment(sketch, "E176.0.3", {"start": v(18.9, 19.1) * mm, "end": v(18.9, 33.79) * mm});
            skArc(sketch, "E176.0.4", {"start": v(18.9, 33.79) * mm, "mid": v(19.14, 34.35) * mm, "end": v(19.7, 34.58) * mm});
            skLineSegment(sketch, "E176.0.5", {"start": v(19.7, 34.58) * mm, "end": v(34.39, 34.58) * mm});
            skArc(sketch, "E176.0.6", {"start": v(34.39, 34.58) * mm, "mid": v(34.5, 34.58) * mm, "end": v(34.6, 34.55) * mm});
            skLineSegment(sketch, "E176.0.7", {"start": v(34.6, 34.55) * mm, "end": v(34.6, 36.17) * mm});
            skLineSegment(sketch, "E176.0.8", {"start": v(34.6, 36.17) * mm, "end": v(19.7, 36.17) * mm});
            skArc(sketch, "E176.0.9", {"start": v(19.7, 36.17) * mm, "mid": v(19.14, 36.4) * mm, "end": v(18.9, 36.96) * mm});
            skLineSegment(sketch, "E176.0.10", {"start": v(18.9, 36.96) * mm, "end": v(18.9, 51.65) * mm});
            skArc(sketch, "E176.0.11", {"start": v(18.9, 51.65) * mm, "mid": v(19.14, 52.21) * mm, "end": v(19.7, 52.44) * mm});
            skLineSegment(sketch, "E176.0.12", {"start": v(19.7, 52.44) * mm, "end": v(34.39, 52.44) * mm});
            skArc(sketch, "E176.0.13", {"start": v(34.39, 52.44) * mm, "mid": v(34.5, 52.44) * mm, "end": v(34.6, 52.41) * mm});
            skLineSegment(sketch, "E176.0.14", {"start": v(34.6, 52.41) * mm, "end": v(34.6, 54.06) * mm});
            skArc(sketch, "E176.0.15", {"start": v(34.6, 54.06) * mm, "mid": v(34.5, 54.04) * mm, "end": v(34.39, 54.03) * mm});
            skLineSegment(sketch, "E176.0.16", {"start": v(34.39, 54.03) * mm, "end": v(19.7, 54.03) * mm});
            skArc(sketch, "E176.0.17", {"start": v(19.7, 54.03) * mm, "mid": v(19.14, 54.26) * mm, "end": v(18.9, 54.82) * mm});
            skLineSegment(sketch, "E176.0.18", {"start": v(18.9, 54.82) * mm, "end": v(18.9, 69.5) * mm});
            skArc(sketch, "E176.0.19", {"start": v(18.9, 69.5) * mm, "mid": v(19.14, 70.07) * mm, "end": v(19.7, 70.3) * mm});
            skLineSegment(sketch, "E176.0.20", {"start": v(19.7, 70.3) * mm, "end": v(34.39, 70.3) * mm});
            skArc(sketch, "E176.0.21", {"start": v(34.39, 70.3) * mm, "mid": v(34.5, 70.3) * mm, "end": v(34.6, 70.27) * mm});
            skLineSegment(sketch, "E176.0.22", {"start": v(34.6, 70.27) * mm, "end": v(34.6, 71.44) * mm});
            skLineSegment(sketch, "E176.0.23", {"start": v(34.6, 71.44) * mm, "end": v(-36.99, 71.44) * mm});
            skLineSegment(sketch, "E176.0.24", {"start": v(-36.99, 71.44) * mm, "end": v(-36.99, -71.44) * mm});
            skLineSegment(sketch, "E176.0.25", {"start": v(-36.99, -71.44) * mm, "end": v(34.6, -71.44) * mm});
            skLineSegment(sketch, "E176.0.26", {"start": v(34.6, -71.44) * mm, "end": v(34.6, -17.38) * mm});
            skArc(sketch, "E176.0.27", {"start": v(34.6, -17.38) * mm, "mid": v(34.5, -17.4) * mm, "end": v(34.39, -17.4) * mm});
            skLineSegment(sketch, "E176.0.28", {"start": v(34.39, -17.4) * mm, "end": v(19.7, -17.4) * mm});
            skArc(sketch, "E176.0.29", {"start": v(19.7, -17.4) * mm, "mid": v(19.14, -17.17) * mm, "end": v(18.9, -16.61) * mm});
            skLineSegment(sketch, "E176.0.30", {"start": v(18.9, -16.61) * mm, "end": v(18.9, -1.93) * mm});
            skArc(sketch, "E176.0.31", {"start": v(18.9, -1.93) * mm, "mid": v(19.14, -1.37) * mm, "end": v(19.7, -1.14) * mm});
            skLineSegment(sketch, "E176.0.32", {"start": v(19.7, -1.14) * mm, "end": v(34.39, -1.14) * mm});
            skArc(sketch, "E176.0.33", {"start": v(34.39, -1.14) * mm, "mid": v(34.5, -1.14) * mm, "end": v(34.6, -1.17) * mm});
            skLineSegment(sketch, "E176.0.34", {"start": v(34.6, -1.17) * mm, "end": v(34.6, 0.48) * mm});
            skArc(sketch, "E176.0.35", {"start": v(34.6, 0.48) * mm, "mid": v(34.5, 0.46) * mm, "end": v(34.39, 0.45) * mm});
            skLineSegment(sketch, "E176.0.36", {"start": v(34.39, 0.45) * mm, "end": v(19.7, 0.45) * mm});
            skArc(sketch, "E176.0.37", {"start": v(19.7, 0.45) * mm, "mid": v(19.14, 0.68) * mm, "end": v(18.9, 1.25) * mm});
            skLineSegment(sketch, "E176.0.38", {"start": v(18.9, 1.25) * mm, "end": v(18.9, 15.93) * mm});
            skArc(sketch, "E176.0.39", {"start": v(18.9, 15.93) * mm, "mid": v(19.14, 16.5) * mm, "end": v(19.7, 16.72) * mm});
            skLineSegment(sketch, "E176.0.40", {"start": v(19.7, 16.72) * mm, "end": v(34.39, 16.72) * mm});
            skArc(sketch, "E176.0.41", {"start": v(34.39, 16.72) * mm, "mid": v(34.5, 16.72) * mm, "end": v(34.6, 16.7) * mm});
            skLineSegment(sketch, "E176.0.42", {"start": v(34.6, 16.7) * mm, "end": v(34.6, 18.34) * mm});
            skLineSegment(sketch, "E177", {"start": v(-36.99, -20.96) * mm, "end": v(-36.99, 71.44) * mm});
            skLineSegment(sketch, "E178", {"start": v(34.6, 71.44) * mm, "end": v(34.6, -20.96) * mm});
            skLineSegment(sketch, "E179.0.0", {"start": v(-19.18, -1.14) * mm, "end": v(-33.87, -1.14) * mm});
            skArc(sketch, "E179.0.1", {"start": v(-33.87, -1.14) * mm, "mid": v(-34.43, -1.37) * mm, "end": v(-34.66, -1.93) * mm});
            skLineSegment(sketch, "E179.0.2", {"start": v(-34.66, -1.93) * mm, "end": v(-34.66, -16.61) * mm});
            skArc(sketch, "E179.0.3", {"start": v(-34.66, -16.61) * mm, "mid": v(-34.43, -17.17) * mm, "end": v(-33.87, -17.4) * mm});
            skLineSegment(sketch, "E179.0.4", {"start": v(-33.87, -17.4) * mm, "end": v(-19.18, -17.4) * mm});
            skArc(sketch, "E179.0.5", {"start": v(-19.18, -17.4) * mm, "mid": v(-18.62, -17.17) * mm, "end": v(-18.39, -16.61) * mm});
            skLineSegment(sketch, "E179.0.6", {"start": v(-18.39, -16.61) * mm, "end": v(-18.39, -1.93) * mm});
            skArc(sketch, "E179.0.7", {"start": v(-18.39, -1.93) * mm, "mid": v(-18.62, -1.37) * mm, "end": v(-19.18, -1.14) * mm});
            skLineSegment(sketch, "E180.0.0", {"start": v(-1.33, -1.14) * mm, "end": v(-16, -1.14) * mm});
            skArc(sketch, "E180.0.1", {"start": v(-16, -1.14) * mm, "mid": v(-16.57, -1.37) * mm, "end": v(-16.8, -1.93) * mm});
            skLineSegment(sketch, "E180.0.2", {"start": v(-16.8, -1.93) * mm, "end": v(-16.8, -16.61) * mm});
            skArc(sketch, "E180.0.3", {"start": v(-16.8, -16.61) * mm, "mid": v(-16.57, -17.17) * mm, "end": v(-16, -17.4) * mm});
            skLineSegment(sketch, "E180.0.4", {"start": v(-16, -17.4) * mm, "end": v(-1.33, -17.4) * mm});
            skArc(sketch, "E180.0.5", {"start": v(-1.33, -17.4) * mm, "mid": v(-0.76, -17.17) * mm, "end": v(-0.53, -16.61) * mm});
            skLineSegment(sketch, "E180.0.6", {"start": v(-0.53, -16.61) * mm, "end": v(-0.53, -1.93) * mm});
            skArc(sketch, "E180.0.7", {"start": v(-0.53, -1.93) * mm, "mid": v(-0.76, -1.37) * mm, "end": v(-1.33, -1.14) * mm});
            skArc(sketch, "E181.0.0", {"start": v(1.05, -16.61) * mm, "mid": v(1.28, -17.17) * mm, "end": v(1.85, -17.4) * mm});
            skLineSegment(sketch, "E181.0.1", {"start": v(1.85, -17.4) * mm, "end": v(16.53, -17.4) * mm});
            skArc(sketch, "E181.0.2", {"start": v(16.53, -17.4) * mm, "mid": v(17.1, -17.17) * mm, "end": v(17.32, -16.61) * mm});
            skLineSegment(sketch, "E181.0.3", {"start": v(17.32, -16.61) * mm, "end": v(17.32, -1.93) * mm});
            skArc(sketch, "E181.0.4", {"start": v(17.32, -1.93) * mm, "mid": v(17.1, -1.37) * mm, "end": v(16.53, -1.14) * mm});
            skLineSegment(sketch, "E181.0.5", {"start": v(16.53, -1.14) * mm, "end": v(1.85, -1.14) * mm});
            skArc(sketch, "E181.0.6", {"start": v(1.85, -1.14) * mm, "mid": v(1.28, -1.37) * mm, "end": v(1.05, -1.93) * mm});
            skLineSegment(sketch, "E181.0.7", {"start": v(1.05, -1.93) * mm, "end": v(1.05, -16.61) * mm});
            skArc(sketch, "E182.0.0", {"start": v(16.53, 0.45) * mm, "mid": v(17.1, 0.68) * mm, "end": v(17.32, 1.25) * mm});
            skLineSegment(sketch, "E182.0.1", {"start": v(17.32, 1.25) * mm, "end": v(17.32, 15.93) * mm});
            skArc(sketch, "E182.0.2", {"start": v(17.32, 15.93) * mm, "mid": v(17.1, 16.5) * mm, "end": v(16.53, 16.72) * mm});
            skLineSegment(sketch, "E182.0.3", {"start": v(16.53, 16.72) * mm, "end": v(1.85, 16.72) * mm});
            skArc(sketch, "E182.0.4", {"start": v(1.85, 16.72) * mm, "mid": v(1.28, 16.5) * mm, "end": v(1.05, 15.93) * mm});
            skLineSegment(sketch, "E182.0.5", {"start": v(1.05, 15.93) * mm, "end": v(1.05, 1.25) * mm});
            skArc(sketch, "E182.0.6", {"start": v(1.05, 1.25) * mm, "mid": v(1.28, 0.68) * mm, "end": v(1.85, 0.45) * mm});
            skLineSegment(sketch, "E182.0.7", {"start": v(1.85, 0.45) * mm, "end": v(16.53, 0.45) * mm});
            skArc(sketch, "E183.0.0", {"start": v(-1.33, 0.45) * mm, "mid": v(-0.76, 0.68) * mm, "end": v(-0.53, 1.25) * mm});
            skLineSegment(sketch, "E183.0.1", {"start": v(-0.53, 1.25) * mm, "end": v(-0.53, 15.93) * mm});
            skArc(sketch, "E183.0.2", {"start": v(-0.53, 15.93) * mm, "mid": v(-0.76, 16.5) * mm, "end": v(-1.33, 16.72) * mm});
            skLineSegment(sketch, "E183.0.3", {"start": v(-1.33, 16.72) * mm, "end": v(-16, 16.72) * mm});
            skArc(sketch, "E183.0.4", {"start": v(-16, 16.72) * mm, "mid": v(-16.57, 16.5) * mm, "end": v(-16.8, 15.93) * mm});
            skLineSegment(sketch, "E183.0.5", {"start": v(-16.8, 15.93) * mm, "end": v(-16.8, 1.25) * mm});
            skArc(sketch, "E183.0.6", {"start": v(-16.8, 1.25) * mm, "mid": v(-16.57, 0.68) * mm, "end": v(-16, 0.45) * mm});
            skLineSegment(sketch, "E183.0.7", {"start": v(-16, 0.45) * mm, "end": v(-1.33, 0.45) * mm});
            skLineSegment(sketch, "E184.0.0", {"start": v(-34.66, 15.93) * mm, "end": v(-34.66, 1.25) * mm});
            skArc(sketch, "E184.0.1", {"start": v(-34.66, 1.25) * mm, "mid": v(-34.43, 0.68) * mm, "end": v(-33.87, 0.45) * mm});
            skLineSegment(sketch, "E184.0.2", {"start": v(-33.87, 0.45) * mm, "end": v(-19.18, 0.45) * mm});
            skArc(sketch, "E184.0.3", {"start": v(-19.18, 0.45) * mm, "mid": v(-18.62, 0.68) * mm, "end": v(-18.39, 1.25) * mm});
            skLineSegment(sketch, "E184.0.4", {"start": v(-18.39, 1.25) * mm, "end": v(-18.39, 15.93) * mm});
            skArc(sketch, "E184.0.5", {"start": v(-18.39, 15.93) * mm, "mid": v(-18.62, 16.5) * mm, "end": v(-19.18, 16.72) * mm});
            skLineSegment(sketch, "E184.0.6", {"start": v(-19.18, 16.72) * mm, "end": v(-33.87, 16.72) * mm});
            skArc(sketch, "E184.0.7", {"start": v(-33.87, 16.72) * mm, "mid": v(-34.43, 16.5) * mm, "end": v(-34.66, 15.93) * mm});
            skArc(sketch, "E185.0.0", {"start": v(-34.66, 19.1) * mm, "mid": v(-34.43, 18.54) * mm, "end": v(-33.87, 18.31) * mm});
            skLineSegment(sketch, "E185.0.1", {"start": v(-33.87, 18.31) * mm, "end": v(-19.18, 18.31) * mm});
            skArc(sketch, "E185.0.2", {"start": v(-19.18, 18.31) * mm, "mid": v(-18.62, 18.54) * mm, "end": v(-18.39, 19.1) * mm});
            skLineSegment(sketch, "E185.0.3", {"start": v(-18.39, 19.1) * mm, "end": v(-18.39, 33.79) * mm});
            skArc(sketch, "E185.0.4", {"start": v(-18.39, 33.79) * mm, "mid": v(-18.62, 34.35) * mm, "end": v(-19.18, 34.58) * mm});
            skLineSegment(sketch, "E185.0.5", {"start": v(-19.18, 34.58) * mm, "end": v(-33.87, 34.58) * mm});
            skArc(sketch, "E185.0.6", {"start": v(-33.87, 34.58) * mm, "mid": v(-34.43, 34.35) * mm, "end": v(-34.66, 33.79) * mm});
            skLineSegment(sketch, "E185.0.7", {"start": v(-34.66, 33.79) * mm, "end": v(-34.66, 19.1) * mm});
            skLineSegment(sketch, "E186.0.0", {"start": v(-1.33, 34.58) * mm, "end": v(-16, 34.58) * mm});
            skArc(sketch, "E186.0.1", {"start": v(-16, 34.58) * mm, "mid": v(-16.57, 34.35) * mm, "end": v(-16.8, 33.79) * mm});
            skLineSegment(sketch, "E186.0.2", {"start": v(-16.8, 33.79) * mm, "end": v(-16.8, 19.1) * mm});
            skArc(sketch, "E186.0.3", {"start": v(-16.8, 19.1) * mm, "mid": v(-16.57, 18.54) * mm, "end": v(-16, 18.31) * mm});
            skLineSegment(sketch, "E186.0.4", {"start": v(-16, 18.31) * mm, "end": v(-1.33, 18.31) * mm});
            skArc(sketch, "E186.0.5", {"start": v(-1.33, 18.31) * mm, "mid": v(-0.76, 18.54) * mm, "end": v(-0.53, 19.1) * mm});
            skLineSegment(sketch, "E186.0.6", {"start": v(-0.53, 19.1) * mm, "end": v(-0.53, 33.79) * mm});
            skArc(sketch, "E186.0.7", {"start": v(-0.53, 33.79) * mm, "mid": v(-0.76, 34.35) * mm, "end": v(-1.33, 34.58) * mm});
            skLineSegment(sketch, "E187.0.0", {"start": v(16.53, 34.58) * mm, "end": v(1.85, 34.58) * mm});
            skArc(sketch, "E187.0.1", {"start": v(1.85, 34.58) * mm, "mid": v(1.28, 34.35) * mm, "end": v(1.05, 33.79) * mm});
            skLineSegment(sketch, "E187.0.2", {"start": v(1.05, 33.79) * mm, "end": v(1.05, 19.1) * mm});
            skArc(sketch, "E187.0.3", {"start": v(1.05, 19.1) * mm, "mid": v(1.28, 18.54) * mm, "end": v(1.85, 18.31) * mm});
            skLineSegment(sketch, "E187.0.4", {"start": v(1.85, 18.31) * mm, "end": v(16.53, 18.31) * mm});
            skArc(sketch, "E187.0.5", {"start": v(16.53, 18.31) * mm, "mid": v(17.1, 18.54) * mm, "end": v(17.32, 19.1) * mm});
            skLineSegment(sketch, "E187.0.6", {"start": v(17.32, 19.1) * mm, "end": v(17.32, 33.79) * mm});
            skArc(sketch, "E187.0.7", {"start": v(17.32, 33.79) * mm, "mid": v(17.1, 34.35) * mm, "end": v(16.53, 34.58) * mm});
            skLineSegment(sketch, "E188.0", {"start": v(-33.87, 16.72) * mm, "end": v(-19.18, 16.72) * mm});
            skLineSegment(sketch, "E189.0.0", {"start": v(16.53, 52.44) * mm, "end": v(1.85, 52.44) * mm});
            skArc(sketch, "E189.0.1", {"start": v(1.85, 52.44) * mm, "mid": v(1.28, 52.21) * mm, "end": v(1.05, 51.65) * mm});
            skLineSegment(sketch, "E189.0.2", {"start": v(1.05, 51.65) * mm, "end": v(1.05, 36.96) * mm});
            skArc(sketch, "E189.0.3", {"start": v(1.05, 36.96) * mm, "mid": v(1.28, 36.4) * mm, "end": v(1.85, 36.17) * mm});
            skLineSegment(sketch, "E189.0.4", {"start": v(1.85, 36.17) * mm, "end": v(16.53, 36.17) * mm});
            skArc(sketch, "E189.0.5", {"start": v(16.53, 36.17) * mm, "mid": v(17.1, 36.4) * mm, "end": v(17.32, 36.96) * mm});
            skLineSegment(sketch, "E189.0.6", {"start": v(17.32, 36.96) * mm, "end": v(17.32, 51.65) * mm});
            skArc(sketch, "E189.0.7", {"start": v(17.32, 51.65) * mm, "mid": v(17.1, 52.21) * mm, "end": v(16.53, 52.44) * mm});
            skLineSegment(sketch, "E190.0.0", {"start": v(-1.33, 52.44) * mm, "end": v(-16, 52.44) * mm});
            skArc(sketch, "E190.0.1", {"start": v(-16, 52.44) * mm, "mid": v(-16.57, 52.21) * mm, "end": v(-16.8, 51.65) * mm});
            skLineSegment(sketch, "E190.0.2", {"start": v(-16.8, 51.65) * mm, "end": v(-16.8, 36.96) * mm});
            skArc(sketch, "E190.0.3", {"start": v(-16.8, 36.96) * mm, "mid": v(-16.57, 36.4) * mm, "end": v(-16, 36.17) * mm});
            skLineSegment(sketch, "E190.0.4", {"start": v(-16, 36.17) * mm, "end": v(-1.33, 36.17) * mm});
            skArc(sketch, "E190.0.5", {"start": v(-1.33, 36.17) * mm, "mid": v(-0.76, 36.4) * mm, "end": v(-0.53, 36.96) * mm});
            skLineSegment(sketch, "E190.0.6", {"start": v(-0.53, 36.96) * mm, "end": v(-0.53, 51.65) * mm});
            skArc(sketch, "E190.0.7", {"start": v(-0.53, 51.65) * mm, "mid": v(-0.76, 52.21) * mm, "end": v(-1.33, 52.44) * mm});
            skLineSegment(sketch, "E191.0.0", {"start": v(-19.18, 52.44) * mm, "end": v(-33.87, 52.44) * mm});
            skArc(sketch, "E191.0.1", {"start": v(-33.87, 52.44) * mm, "mid": v(-34.43, 52.21) * mm, "end": v(-34.66, 51.65) * mm});
            skLineSegment(sketch, "E191.0.2", {"start": v(-34.66, 51.65) * mm, "end": v(-34.66, 36.96) * mm});
            skArc(sketch, "E191.0.3", {"start": v(-34.66, 36.96) * mm, "mid": v(-34.43, 36.4) * mm, "end": v(-33.87, 36.17) * mm});
            skLineSegment(sketch, "E191.0.4", {"start": v(-33.87, 36.17) * mm, "end": v(-19.18, 36.17) * mm});
            skArc(sketch, "E191.0.5", {"start": v(-19.18, 36.17) * mm, "mid": v(-18.62, 36.4) * mm, "end": v(-18.39, 36.96) * mm});
            skLineSegment(sketch, "E191.0.6", {"start": v(-18.39, 36.96) * mm, "end": v(-18.39, 51.65) * mm});
            skArc(sketch, "E191.0.7", {"start": v(-18.39, 51.65) * mm, "mid": v(-18.62, 52.21) * mm, "end": v(-19.18, 52.44) * mm});
            skLineSegment(sketch, "E192.0.0", {"start": v(16.53, 70.3) * mm, "end": v(1.85, 70.3) * mm});
            skArc(sketch, "E192.0.1", {"start": v(1.85, 70.3) * mm, "mid": v(1.28, 70.07) * mm, "end": v(1.05, 69.5) * mm});
            skLineSegment(sketch, "E192.0.2", {"start": v(1.05, 69.5) * mm, "end": v(1.05, 54.82) * mm});
            skArc(sketch, "E192.0.3", {"start": v(1.05, 54.82) * mm, "mid": v(1.28, 54.26) * mm, "end": v(1.85, 54.03) * mm});
            skLineSegment(sketch, "E192.0.4", {"start": v(1.85, 54.03) * mm, "end": v(16.53, 54.03) * mm});
            skArc(sketch, "E192.0.5", {"start": v(16.53, 54.03) * mm, "mid": v(17.1, 54.26) * mm, "end": v(17.32, 54.82) * mm});
            skLineSegment(sketch, "E192.0.6", {"start": v(17.32, 54.82) * mm, "end": v(17.32, 69.5) * mm});
            skArc(sketch, "E192.0.7", {"start": v(17.32, 69.5) * mm, "mid": v(17.1, 70.07) * mm, "end": v(16.53, 70.3) * mm});
            skArc(sketch, "E193.0.0", {"start": v(-0.53, 69.5) * mm, "mid": v(-0.76, 70.07) * mm, "end": v(-1.33, 70.3) * mm});
            skLineSegment(sketch, "E193.0.1", {"start": v(-1.33, 70.3) * mm, "end": v(-16, 70.3) * mm});
            skArc(sketch, "E193.0.2", {"start": v(-16, 70.3) * mm, "mid": v(-16.57, 70.07) * mm, "end": v(-16.8, 69.5) * mm});
            skLineSegment(sketch, "E193.0.3", {"start": v(-16.8, 69.5) * mm, "end": v(-16.8, 54.82) * mm});
            skArc(sketch, "E193.0.4", {"start": v(-16.8, 54.82) * mm, "mid": v(-16.57, 54.26) * mm, "end": v(-16, 54.03) * mm});
            skLineSegment(sketch, "E193.0.5", {"start": v(-16, 54.03) * mm, "end": v(-1.33, 54.03) * mm});
            skArc(sketch, "E193.0.6", {"start": v(-1.33, 54.03) * mm, "mid": v(-0.76, 54.26) * mm, "end": v(-0.53, 54.82) * mm});
            skLineSegment(sketch, "E193.0.7", {"start": v(-0.53, 54.82) * mm, "end": v(-0.53, 69.5) * mm});
            skArc(sketch, "E194.0.0", {"start": v(-18.39, 69.5) * mm, "mid": v(-18.62, 70.07) * mm, "end": v(-19.18, 70.3) * mm});
            skLineSegment(sketch, "E194.0.1", {"start": v(-19.18, 70.3) * mm, "end": v(-33.87, 70.3) * mm});
            skArc(sketch, "E194.0.2", {"start": v(-33.87, 70.3) * mm, "mid": v(-34.43, 70.07) * mm, "end": v(-34.66, 69.5) * mm});
            skLineSegment(sketch, "E194.0.3", {"start": v(-34.66, 69.5) * mm, "end": v(-34.66, 54.82) * mm});
            skArc(sketch, "E194.0.4", {"start": v(-34.66, 54.82) * mm, "mid": v(-34.43, 54.26) * mm, "end": v(-33.87, 54.03) * mm});
            skLineSegment(sketch, "E194.0.5", {"start": v(-33.87, 54.03) * mm, "end": v(-19.18, 54.03) * mm});
            skArc(sketch, "E194.0.6", {"start": v(-19.18, 54.03) * mm, "mid": v(-18.62, 54.26) * mm, "end": v(-18.39, 54.82) * mm});
            skLineSegment(sketch, "E194.0.7", {"start": v(-18.39, 54.82) * mm, "end": v(-18.39, 69.5) * mm});
            skLineSegment(sketch, "E195.0", {"start": v(-16.8, 36.96) * mm, "end": v(-16.8, 51.65) * mm});
            skSolve(sketch);
        }
        {
            var Q0;
            {var subQ0=sQuery(id+"F10.wireOp",EDGE,"E175");Q0=makeQuery(id+"F10.imprint","IMPRINT",FACE,{"disambiguationData":[TD([[makeQuery(id+"F10.imprint","IMPRINT",EDGE,{"derivedFrom":subQ0}),1.0]])]});}
            extrude(context, id + "F11", {"entities" : qUnion([Q0]), "operationType" : NewBodyOperationType.ADD, "depth" : 1.59 * mm});
        }
        {
            var Q0;
            Q0=makeQuery(id+"F1.opExtrude","SWEPT_FACE",FACE,{"disambiguationData":[OSD([sQuery(id+"F0.wireOp",EDGE,"E0.right")])]});
            var sketch = newSketch(context, id + "F12", { "sketchPlane" : qUnion([Q0])});
            skLineSegment(sketch, "E196.0.0", {"start": v(71.44, 3.97) * mm, "end": v(-71.44, 3.97) * mm});
            skLineSegment(sketch, "E196.0.1", {"start": v(-71.44, 3.97) * mm, "end": v(-71.44, 0) * mm});
            skLineSegment(sketch, "E196.0.2", {"start": v(-71.44, 0) * mm, "end": v(71.44, 0) * mm});
            skLineSegment(sketch, "E196.0.3", {"start": v(71.44, 0) * mm, "end": v(71.44, 3.97) * mm});
            skLineSegment(sketch, "E197.0.0", {"start": v(-71.44, 0) * mm, "end": v(-74.61, 0) * mm});
            skLineSegment(sketch, "E197.0.1", {"start": v(-71.44, 0) * mm, "end": v(-71.44, 3.97) * mm});
            skLineSegment(sketch, "E197.0.2", {"start": v(-71.44, 3.97) * mm, "end": v(-74.61, 3.97) * mm});
            skLineSegment(sketch, "E197.0.3", {"start": v(-74.61, 0) * mm, "end": v(-74.61, 3.97) * mm});
            skLineSegment(sketch, "E198", {"start": v(-74.61, 1.98) * mm, "end": v(-45.32, 1.98) * mm});
            skLineSegment(sketch, "E199", {"start": v(-45.32, 1.98) * mm, "end": v(-45.32, 0) * mm});
            skLineSegment(sketch, "E200.bottom", {"start": v(-38.97, -5.56) * mm, "end": v(-51.67, -5.56) * mm});
            skLineSegment(sketch, "E200.top", {"start": v(-38.97, 5.56) * mm, "end": v(-51.67, 5.56) * mm});
            skLineSegment(sketch, "E200.left", {"start": v(-38.97, -5.56) * mm, "end": v(-38.97, 5.56) * mm});
            skLineSegment(sketch, "E200.right", {"start": v(-51.67, -5.56) * mm, "end": v(-51.67, 5.56) * mm});
            skPoint(sketch, "E200.middle", {"position": v(-45.32, 0) * mm});
            skLineSegment(sketch, "E201.bottom", {"start": v(-51.67, 5.56) * mm, "end": v(-38.97, 5.56) * mm});
            skLineSegment(sketch, "E201.top", {"start": v(-51.67, 0) * mm, "end": v(-38.97, 0) * mm});
            skLineSegment(sketch, "E201.left", {"start": v(-51.67, 5.56) * mm, "end": v(-51.67, 0) * mm});
            skLineSegment(sketch, "E201.right", {"start": v(-38.97, 5.56) * mm, "end": v(-38.97, 0) * mm});
            skSolve(sketch);
        }
        {
            var Q0;
            {var subQ1=sQuery(id+"F12.wireOp",EDGE,"E199");Q0=makeQuery(id+"F12.imprint","IMPRINT",FACE,{"disambiguationData":[TD([[makeQuery(id+"F12.imprint","IMPRINT",EDGE,{"derivedFrom":subQ1}),1.0]])]});}
            var Q1;
            {var subQ0=sQuery(id+"F12.wireOp",EDGE,"E199");Q1=makeQuery(id+"F12.imprint","IMPRINT",FACE,{"disambiguationData":[TD([[makeQuery(id+"F12.imprint","IMPRINT",EDGE,{"derivedFrom":subQ0}),-1.0]])]});}
            var Q2;
            {var subQ5=sQuery(id+"F12.wireOp",EDGE,"E201.bottom");Q2=makeQuery(id+"F12.imprint","IMPRINT",FACE,{"disambiguationData":[TD([[makeQuery(id+"F12.imprint","IMPRINT",EDGE,{"derivedFrom":subQ5}),-1.0]])]});}
            extrude(context, id + "F13", {"entities" : qUnion([Q0, Q1, Q2]), "operationType" : NewBodyOperationType.REMOVE, "oppositeDirection" : true, "depth" : 6.35 * mm});
        }
    });
